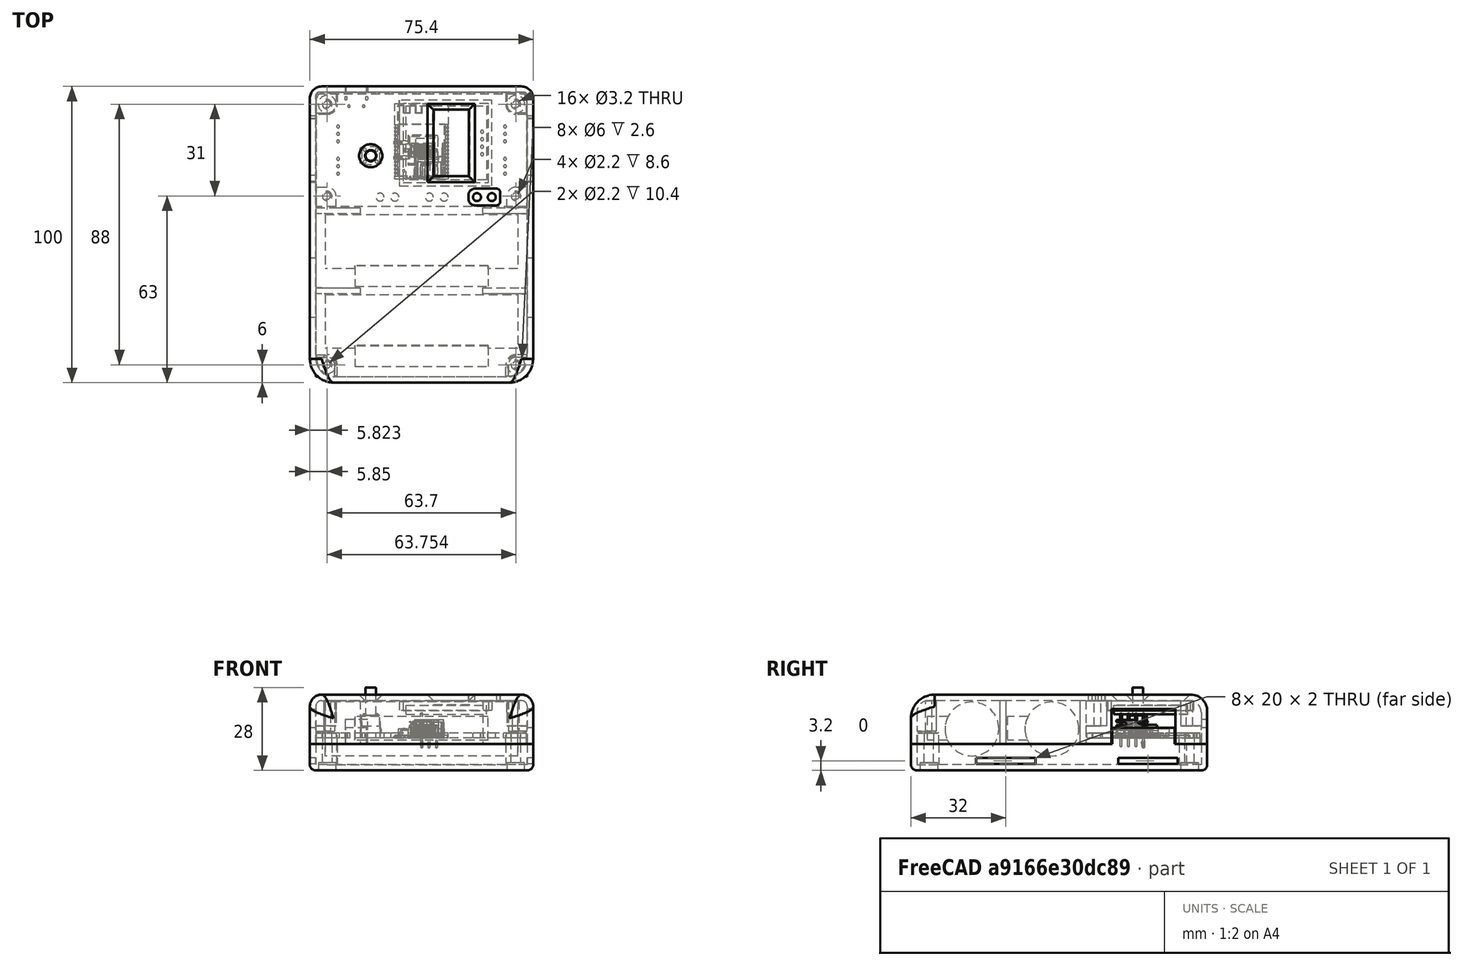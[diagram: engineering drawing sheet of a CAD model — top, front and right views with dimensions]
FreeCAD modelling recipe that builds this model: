
FCSTD DOCUMENT  (FreeCAD 0.21R33694 (Git))
Label: rwled
License: All rights reserved
LicenseURL: http://en.wikipedia.org/wiki/All_rights_reserved
objects: Part::Feature×61, App::Part×48, Sketcher::SketchObject×29, PartDesign::Pad×17, PartDesign::Pocket×12, PartDesign::Fillet×11, PartDesign::Body×6, Part::Part2DObjectPython×1, Mesh::Feature×1, App::DocumentObjectGroup×1
note: 177 computed .brp shape members not serialized (recipe doc carries the construction recipe); baked Part::Feature solids carry a one-line shape summary decoded from their .brp

FEATURE [Sketcher::SketchObject] Sketch
  FullyConstrained = true
  MapMode = 5
  Support = -> [XY_Plane043]
  sketch-geometry (4):
    g0: LineSegment StartX=-37.7 StartY=21.5 StartZ=0 EndX=37.7 EndY=21.5 EndZ=0
    g1: LineSegment StartX=37.7 StartY=21.5 StartZ=0 EndX=37.7 EndY=-78.5 EndZ=0
    g2: LineSegment StartX=37.7 StartY=-78.5 StartZ=0 EndX=-37.7 EndY=-78.5 EndZ=0
    g3: LineSegment StartX=-37.7 StartY=-78.5 StartZ=0 EndX=-37.7 EndY=21.5 EndZ=0
  constraints (11):
    c: Coincident(g0,g1)
    c: Coincident(g1,g2)
    c: Coincident(g2,g3)
    c: Coincident(g3,g0)
    c: Horizontal(g2)
    c: Vertical(g1)
    c: Vertical(g3)
    c: Symmetric(g0,g0,g-2)
    c: Distance(g0) = 75.4
    c: Distance(g0,g-1) = 21.5
    c: DistanceY(g3,g3) = 100
FEATURE [Part::Feature] Part__Feature049  label="Micro USB-B Female 5Pin SMD"
  shape: bbox 0.3 x 1.55 x 4.2 mm, 15 faces (baked)
FEATURE [Part::Feature] Part__Feature050  label="Micro USB-B Female 5Pin SMD001"
  shape: bbox 0.3 x 1.55 x 4.2 mm, 15 faces (baked)
FEATURE [Part::Feature] Part__Feature051  label="Micro USB-B Female 5Pin SMD002"
  shape: bbox 0.3 x 1.55 x 4.2 mm, 15 faces (baked)
FEATURE [Part::Feature] Part__Feature052  label="Micro USB-B Female 5Pin SMD003"
  shape: bbox 0.3 x 1.55 x 4.2 mm, 15 faces (baked)
FEATURE [Part::Feature] Part__Feature053  label="Micro USB-B Female 5Pin SMD004"
  shape: bbox 0.3 x 1.55 x 4.2 mm, 15 faces (baked)
FEATURE [Part::Feature] Part__Feature054  label="Micro USB-B Female 5Pin SMD005"
  shape: bbox 6.9 x 2.4 x 4.15 mm, 176 faces (baked)
FEATURE [Part::Feature] Part__Feature055  label="Micro USB-B Female 5Pin SMD006"
  shape: bbox 8.172 x 3.786 x 5.619 mm, 257 faces (baked)
FEATURE [App::Part] Micro_USB_B_Female_5Pin_SMD  label="Micro USB-B Female 5Pin SMD007"
  Group = -> [Part__Feature049,Part__Feature050,Part__Feature051,Part__Feature052,Part__Feature053,Part__Feature054,Part__Feature055]
  Origin = -> Origin087
  Placement = pos=(-22,14.6,4.85) rot=(0,1,1;3.14159rad)
FEATURE [Part::Feature] Part__Feature056  label="SW_PUSH_6mm_h13mm"
  Placement = pos=(-20.29,0.35,4) rot=(0,0,1;0rad)
  shape: bbox 7.174 x 6 x 16.5 mm, 105 faces (baked)
FEATURE [PartDesign::Pad] Pad
  Direction = (0,0,1)
  Length = 16.6
  Length2 = 10
  Profile = -> Sketch
  ReferenceAxis = -> Sketch [N_Axis]
  Type = 0
FEATURE [Sketcher::SketchObject] Sketch001
  FullyConstrained = true
  MapMode = 5
  Placement = pos=(0,0,0) rot=(0.57735,0.57735,0.57735;2.0944rad)
  Support = -> [YZ_Plane088]
  sketch-geometry (1):
    g0: Circle CenterX=9.1 CenterY=0 CenterZ=0 NormalX=0 NormalY=0 NormalZ=1 AngleXU=0 Radius=9.1
  constraints (3):
    c: PointOnObject(g0,g-1)
    c: Distance(g-1,g0) = 9.1
    c: PointOnObject(g-1,g0)
FEATURE [PartDesign::Pad] Pad001
  Direction = (1,-2e-16,3e-16)
  Length = 65
  Length2 = 10
  Placement = pos=(0,0,0) rot=(0.57735,0.57735,0.57735;2.0944rad)
  Profile = -> Sketch001
  ReferenceAxis = -> Sketch001 [N_Axis]
  Type = 0
FEATURE [Sketcher::SketchObject] Sketch002
  FullyConstrained = false
  MapMode = 5
  Placement = pos=(0,0,0) rot=(1,0,0;1.5708rad)
  Support = -> [XZ_Plane088]
  sketch-geometry (4):
    g0: LineSegment StartX=10 StartY=-3.77048 StartZ=0 EndX=55 EndY=-3.77048 EndZ=0
    g1: LineSegment StartX=55 StartY=-3.77048 StartZ=0 EndX=55 EndY=4.22952 EndZ=0
    g2: LineSegment StartX=55 StartY=4.22952 StartZ=0 EndX=10 EndY=4.22952 EndZ=0
    g3: LineSegment StartX=10 StartY=4.22952 StartZ=0 EndX=10 EndY=-3.77048 EndZ=0
  constraints (11):
    c: Coincident(g0,g1)
    c: Coincident(g1,g2)
    c: Coincident(g2,g3)
    c: Coincident(g3,g0)
    c: Horizontal(g0)
    c: Horizontal(g2)
    c: Vertical(g1)
    c: Vertical(g3)
    c: DistanceX(g-1,g0) = 10
    c: DistanceX(g2,g2) = 45
    c: DistanceY(g3,g3) = 8
FEATURE [PartDesign::Pad] Pad002
  BaseFeature = -> Pad001
  Direction = (0,-1,2e-16)
  Length = 6
  Length2 = 10
  Placement = pos=(0,0,0) rot=(0.57735,0.57735,0.57735;2.0944rad)
  Profile = -> Sketch002
  ReferenceAxis = -> Sketch002 [N_Axis]
  Type = 4
FEATURE [PartDesign::Body] Body001  label="accum-a"
  Group = -> [Sketch001,Pad001,Sketch002,Pad002]
  Origin = -> Origin088
  Placement = pos=(-32.5,-40,3) rot=(0,0,1;0rad)
  Tip = -> Pad002
FEATURE [Sketcher::SketchObject] Sketch003
  FullyConstrained = true
  MapMode = 5
  Placement = pos=(0,0,0) rot=(0.57735,0.57735,0.57735;2.0944rad)
  Support = -> [YZ_Plane090]
  sketch-geometry (1):
    g0: Circle CenterX=9.1 CenterY=0 CenterZ=0 NormalX=0 NormalY=0 NormalZ=1 AngleXU=0 Radius=9.1
  constraints (3):
    c: PointOnObject(g0,g-1)
    c: Distance(g-1,g0) = 9.1
    c: PointOnObject(g-1,g0)
FEATURE [PartDesign::Pad] Pad003
  Direction = (1,-2e-16,3e-16)
  Length = 65
  Length2 = 10
  Placement = pos=(0,0,0) rot=(0.57735,0.57735,0.57735;2.0944rad)
  Profile = -> Sketch003
  ReferenceAxis = -> Sketch003 [N_Axis]
  Type = 0
FEATURE [Sketcher::SketchObject] Sketch004
  FullyConstrained = false
  MapMode = 5
  Placement = pos=(0,0,0) rot=(1,0,0;1.5708rad)
  Support = -> [XZ_Plane090]
  sketch-geometry (4):
    g0: LineSegment StartX=10 StartY=-3.77048 StartZ=0 EndX=55 EndY=-3.77048 EndZ=0
    g1: LineSegment StartX=55 StartY=-3.77048 StartZ=0 EndX=55 EndY=4.22952 EndZ=0
    g2: LineSegment StartX=55 StartY=4.22952 StartZ=0 EndX=10 EndY=4.22952 EndZ=0
    g3: LineSegment StartX=10 StartY=4.22952 StartZ=0 EndX=10 EndY=-3.77048 EndZ=0
  constraints (11):
    c: Coincident(g0,g1)
    c: Coincident(g1,g2)
    c: Coincident(g2,g3)
    c: Coincident(g3,g0)
    c: Horizontal(g0)
    c: Horizontal(g2)
    c: Vertical(g1)
    c: Vertical(g3)
    c: DistanceX(g-1,g0) = 10
    c: DistanceX(g2,g2) = 45
    c: DistanceY(g3,g3) = 8
FEATURE [PartDesign::Pad] Pad004
  BaseFeature = -> Pad003
  Direction = (0,-1,2e-16)
  Length = 6
  Length2 = 10
  Placement = pos=(0,0,0) rot=(0.57735,0.57735,0.57735;2.0944rad)
  Profile = -> Sketch004
  ReferenceAxis = -> Sketch004 [N_Axis]
  Type = 4
FEATURE [PartDesign::Body] Body003  label="accum-b"
  Group = -> [Sketch003,Pad003,Sketch004,Pad004]
  Origin = -> Origin090
  Placement = pos=(-32.5,-67,3) rot=(0,0,1;0rad)
  Tip = -> Pad004
FEATURE [Sketcher::SketchObject] Sketch005
  ExternalGeometry = -> [Pad]
  FullyConstrained = true
  MapMode = 5
  Placement = pos=(0,0,0) rot=(1,0,0;3.14159rad)
  Support = -> [Pad]
  sketch-geometry (4):
    g0: LineSegment StartX=-35.7 StartY=76.5 StartZ=0 EndX=35.7 EndY=76.5 EndZ=0
    g1: LineSegment StartX=35.7 StartY=76.5 StartZ=0 EndX=35.7 EndY=-19.5 EndZ=0
    g2: LineSegment StartX=35.7 StartY=-19.5 StartZ=0 EndX=-35.7 EndY=-19.5 EndZ=0
    g3: LineSegment StartX=-35.7 StartY=-19.5 StartZ=0 EndX=-35.7 EndY=76.5 EndZ=0
  constraints (11):
    c: Coincident(g0,g1)
    c: Coincident(g1,g2)
    c: Coincident(g2,g3)
    c: Coincident(g3,g0)
    c: Horizontal(g2)
    c: Vertical(g1)
    c: Vertical(g3)
    c: DistanceX(g0,g0) = 71.4
    c: DistanceY(g3,g3) = 96
    c: Symmetric(g0,g0,g-2)
    c: DistanceY(g0,g-3) = 2
FEATURE [PartDesign::Pocket] Pocket
  BaseFeature = -> Pad
  Direction = (0,0,1)
  Length = 14.6
  Length2 = 5
  Profile = -> Sketch005
  ReferenceAxis = -> Sketch005 [N_Axis]
  Type = 0
FEATURE [Sketcher::SketchObject] Sketch006
  FullyConstrained = true
  MapMode = 5
  Placement = pos=(37.7,0,0) rot=(0.57735,0.57735,0.57735;2.0944rad)
  Support = -> [Pocket]
  sketch-geometry (4):
    g0: LineSegment StartX=-10.8 StartY=11.8 StartZ=0 EndX=10.8 EndY=11.8 EndZ=0
    g1: LineSegment StartX=10.8 StartY=11.8 StartZ=0 EndX=10.8 EndY=0 EndZ=0
    g2: LineSegment StartX=10.8 StartY=0 StartZ=0 EndX=-10.8 EndY=0 EndZ=0
    g3: LineSegment StartX=-10.8 StartY=0 StartZ=0 EndX=-10.8 EndY=11.8 EndZ=0
  constraints (12):
    c: Coincident(g0,g1)
    c: Coincident(g1,g2)
    c: Coincident(g2,g3)
    c: Coincident(g3,g0)
    c: Horizontal(g0)
    c: Horizontal(g2)
    c: Vertical(g1)
    c: Vertical(g3)
    c: DistanceX(g0,g0) = 21.6
    c: DistanceY(g3,g3) = 11.8
    c: Distance(g2,g-2) = 10.8
    c: PointOnObject(g-1,g2)
FEATURE [PartDesign::Pocket] Pocket001  label="Отверстие разъёмы справа"
  BaseFeature = -> Pocket
  Direction = (-1,0,0)
  Length = 2
  Length2 = 5
  Profile = -> Sketch006
  ReferenceAxis = -> Sketch006 [N_Axis]
  Type = 0
FEATURE [Sketcher::SketchObject] Sketch007
  FullyConstrained = true
  MapMode = 5
  Placement = pos=(-37.7,0,0) rot=(0.57735,-0.57735,-0.57735;2.0944rad)
  Support = -> [Pocket]
  sketch-geometry (4):
    g0: LineSegment StartX=-10.8 StartY=11.8 StartZ=0 EndX=10.8 EndY=11.8 EndZ=0
    g1: LineSegment StartX=10.8 StartY=11.8 StartZ=0 EndX=10.8 EndY=0 EndZ=0
    g2: LineSegment StartX=10.8 StartY=0 StartZ=0 EndX=-10.8 EndY=0 EndZ=0
    g3: LineSegment StartX=-10.8 StartY=0 StartZ=0 EndX=-10.8 EndY=11.8 EndZ=0
  constraints (12):
    c: Coincident(g0,g1)
    c: Coincident(g1,g2)
    c: Coincident(g2,g3)
    c: Coincident(g3,g0)
    c: Horizontal(g0)
    c: Horizontal(g2)
    c: Vertical(g1)
    c: Vertical(g3)
    c: DistanceX(g0,g0) = 21.6
    c: DistanceY(g3,g3) = 11.8
    c: Distance(g1,g-2) = 10.8
    c: PointOnObject(g-1,g2)
FEATURE [PartDesign::Pocket] Pocket002  label="Отверстие разъёмы слева"
  BaseFeature = -> Pocket001
  Direction = (1,0,0)
  Length = 2
  Length2 = 5
  Profile = -> Sketch007
  ReferenceAxis = -> Sketch007 [N_Axis]
  Type = 2
FEATURE [Sketcher::SketchObject] Sketch008
  ExternalGeometry = -> [Pocket]
  FullyConstrained = true
  MapMode = 5
  Placement = pos=(0,21.5,0) rot=(0,0.707107,0.707107;3.14159rad)
  Support = -> [Pocket]
  sketch-geometry (4):
    g0: LineSegment StartX=18.2 StartY=8.2 StartZ=0 EndX=25.8 EndY=8.2 EndZ=0
    g1: LineSegment StartX=25.8 StartY=8.2 StartZ=0 EndX=25.8 EndY=0 EndZ=0
    g2: LineSegment StartX=25.8 StartY=0 StartZ=0 EndX=18.2 EndY=0 EndZ=0
    g3: LineSegment StartX=18.2 StartY=0 StartZ=0 EndX=18.2 EndY=8.2 EndZ=0
  constraints (12):
    c: Coincident(g0,g1)
    c: Coincident(g1,g2)
    c: Coincident(g2,g3)
    c: Coincident(g3,g0)
    c: Horizontal(g0)
    c: Horizontal(g2)
    c: Vertical(g1)
    c: Vertical(g3)
    c: PointOnObject(g1,g-1)
    c: Distance(g-3,g1) = 11.9
    c: DistanceX(g0,g0) = 7.6
    c: DistanceY(g3,g3) = 8.2
FEATURE [PartDesign::Pocket] Pocket003  label="Отверстие usb"
  BaseFeature = -> Pocket002
  Direction = (0,-1,2e-16)
  Length = 2
  Length2 = 5
  Profile = -> Sketch008
  ReferenceAxis = -> Sketch008 [N_Axis]
  Type = 0
FEATURE [Sketcher::SketchObject] Sketch009
  FullyConstrained = false
  MapMode = 5
  Placement = pos=(0,0,16.6) rot=(0,0,1;0rad)
  Support = -> [Pocket]
  sketch-geometry (8):
    g0: LineSegment StartX=15.8257 StartY=-15.3377 StartZ=0 EndX=15.8257 EndY=-16.3217 EndZ=0
    g1: LineSegment StartX=26.545 StartY=-14.2196 StartZ=0 EndX=26.545 EndY=-17.3559 EndZ=0
    g2: LineSegment StartX=17.9219 StartY=-13.0027 StartZ=0 EndX=25.2742 EndY=-13.0027 EndZ=0
    g3: LineSegment StartX=17.897 StartY=-18.6636 StartZ=0 EndX=25.2824 EndY=-18.6636 EndZ=0
    g4: ArcOfCircle CenterX=18.1168 CenterY=-15.2861 CenterZ=0 NormalX=0 NormalY=0 NormalZ=1 AngleXU=0 Radius=2.29165 StartAngle=1.65595 EndAngle=3.16413
    g5: ArcOfCircle CenterX=18.1087 CenterY=-16.3895 CenterZ=0 NormalX=0 NormalY=0 NormalZ=1 AngleXU=0 Radius=2.28395 StartAngle=3.11191 EndAngle=4.61961
    g6: ArcOfCircle CenterX=25.295 CenterY=-14.253 CenterZ=0 NormalX=0 NormalY=0 NormalZ=1 AngleXU=0 Radius=1.25044 StartAngle=0.026699 EndAngle=1.58738
    g7: ArcOfCircle CenterX=25.2642 CenterY=-17.3827 CenterZ=0 NormalX=0 NormalY=0 NormalZ=1 AngleXU=0 Radius=1.28106 StartAngle=4.7266 EndAngle=6.30404
  constraints (12):
    c: Vertical(g0)
    c: Vertical(g1)
    c: Horizontal(g2)
    c: Horizontal(g3)
    c: Coincident(g4,g0)
    c: Coincident(g4,g2)
    c: Coincident(g5,g0)
    c: Coincident(g5,g3)
    c: Coincident(g6,g2)
    c: Coincident(g6,g1)
    c: Coincident(g7,g1)
    c: Coincident(g7,g3)
FEATURE [PartDesign::Pocket] Pocket004  label="Отверстия индикация"
  BaseFeature = -> Pocket003
  Direction = (0,0,-1)
  Length = 2
  Length2 = 5
  Profile = -> Sketch009
  ReferenceAxis = -> Sketch009 [N_Axis]
  Type = 0
FEATURE [Sketcher::SketchObject] Sketch010
  FullyConstrained = false
  MapMode = 5
  Placement = pos=(0,0,16.6) rot=(0,0,1;0rad)
  Support = -> [Pocket]
  sketch-geometry (7):
    g0: Circle CenterX=-17.1458 CenterY=-1.90076 CenterZ=0 NormalX=0 NormalY=0 NormalZ=1 AngleXU=0 Radius=3.9
    g1: GeomPoint X=-17.1369 Y=-1.89872 Z=0
    g2: GeomPoint X=-17.1369 Y=-1.89872 Z=0
    g3: LineSegment StartX=2 StartY=15.65 StartZ=0 EndX=18 EndY=15.65 EndZ=0
    g4: LineSegment StartX=18 StartY=15.65 StartZ=0 EndX=18 EndY=-10.85 EndZ=0
    g5: LineSegment StartX=18 StartY=-10.85 StartZ=0 EndX=2 EndY=-10.85 EndZ=0
    g6: LineSegment StartX=2 StartY=-10.85 StartZ=0 EndX=2 EndY=15.65 EndZ=0
  constraints (14):
    c: Diameter(g0) = 7.8
    c: Coincident(g2,g1)
    c: Coincident(g3,g4)
    c: Coincident(g4,g5)
    c: Coincident(g5,g6)
    c: Coincident(g6,g3)
    c: Horizontal(g3)
    c: Horizontal(g5)
    c: Vertical(g4)
    c: Vertical(g6)
    c: DistanceX(g3,g3) = 16
    c: DistanceY(g6,g6) = 26.5
    c: DistanceY(g5,g-1) = 10.85
    c: DistanceX(g-1,g5) = 2
FEATURE [Part::Part2DObjectPython] Circle  # Draft 2D object (typed FeaturePython)
  Area = 0.502819
  FirstAngle = 0
  LastAngle = 0
  MakeFace = true
  Placement = pos=(-17.14,-1.9,15) rot=(0,0,1;1.5708rad)
  Radius = 0.400065
FEATURE [PartDesign::Pocket] Pocket005  label="Отверстие кнопка (конус)"
  BaseFeature = -> Pocket004
  Direction = (0,0,-1)
  Length = 2
  Length2 = 5
  Profile = -> Sketch010
  ReferenceAxis = -> Sketch010 [N_Axis]
  TaperAngle = -45
  Type = 0
FEATURE [Sketcher::SketchObject] Sketch011
  ExternalGeometry = -> [Pocket]
  FullyConstrained = false
  MapMode = 5
  Placement = pos=(0,0,14.6) rot=(1,0,0;3.14159rad)
  Support = -> [Pocket]
  sketch-geometry (18):
    g0: LineSegment StartX=-35.7 StartY=46.5 StartZ=0 EndX=-20.7 EndY=46.5 EndZ=0
    g1: LineSegment StartX=-20.7 StartY=46.5 StartZ=0 EndX=-20.7 EndY=48.5 EndZ=0
    g2: LineSegment StartX=-20.7 StartY=48.5 StartZ=0 EndX=-35.7 EndY=48.5 EndZ=0
    g3: LineSegment StartX=-35.7 StartY=48.5 StartZ=0 EndX=-35.7 EndY=46.5 EndZ=0
    g4: LineSegment StartX=-35.7 StartY=19.5 StartZ=0 EndX=-20.7 EndY=19.5 EndZ=0
    g5: LineSegment StartX=-20.7 StartY=19.5 StartZ=0 EndX=-20.7 EndY=21.5 EndZ=0
    g6: LineSegment StartX=-20.7 StartY=21.5 StartZ=0 EndX=-35.7 EndY=21.5 EndZ=0
    g7: LineSegment StartX=-35.7 StartY=21.5 StartZ=0 EndX=-35.7 EndY=19.5 EndZ=0
    g8: LineSegment StartX=35.7 StartY=48.5 StartZ=0 EndX=20.7 EndY=48.5 EndZ=0
    g9: LineSegment StartX=20.7 StartY=48.5 StartZ=0 EndX=20.7 EndY=46.5 EndZ=0
    g10: LineSegment StartX=20.7 StartY=46.5 StartZ=0 EndX=35.7 EndY=46.5 EndZ=0
    g11: LineSegment StartX=35.7 StartY=46.5 StartZ=0 EndX=35.7 EndY=48.5 EndZ=0
    g12: LineSegment StartX=35.7 StartY=21.5 StartZ=0 EndX=20.7 EndY=21.5 EndZ=0
    g13: LineSegment StartX=20.7 StartY=21.5 StartZ=0 EndX=20.7 EndY=19.5 EndZ=0
    g14: LineSegment StartX=20.7 StartY=19.5 StartZ=0 EndX=35.7 EndY=19.5 EndZ=0
    g15: LineSegment StartX=35.7 StartY=19.5 StartZ=0 EndX=35.7 EndY=21.5 EndZ=0
    g16: GeomPoint X=-35.7 Y=47.5 Z=0
    g17: GeomPoint X=35.7 Y=47.5 Z=0
  constraints (48):
    c: Coincident(g0,g1)
    c: Coincident(g1,g2)
    c: Coincident(g2,g3)
    c: Coincident(g3,g0)
    c: Horizontal(g0)
    c: Horizontal(g2)
    c: Vertical(g1)
    c: Vertical(g3)
    c: PointOnObject(g0,g-3)
    c: Coincident(g4,g5)
    c: Coincident(g5,g6)
    c: Coincident(g6,g7)
    c: Coincident(g7,g4)
    c: Horizontal(g4)
    c: Horizontal(g6)
    c: Vertical(g5)
    c: Vertical(g7)
    c: Distance(g4,g5) = 2
    c: Distance(g0,g1) = 2
    c: Distance(g6) = 15
    c: Distance(g0) = 15
    c: Coincident(g8,g9)
    c: Coincident(g9,g10)
    c: Coincident(g10,g11)
    c: Coincident(g11,g8)
    c: Horizontal(g8)
    c: Horizontal(g10)
    c: Vertical(g9)
    c: Vertical(g11)
    c: PointOnObject(g8,g-4)
    c: Coincident(g12,g13)
    c: Coincident(g13,g14)
    c: Coincident(g14,g15)
    c: Coincident(g15,g12)
    c: Horizontal(g12)
    c: Horizontal(g14)
    c: Vertical(g13)
    c: Vertical(g15)
    c: Distance(g9) = 2
    c: Distance(g13) = 2
    c: Distance(g12) = 15
    c: Distance(g10) = 15
    c: Distance(g-3,g4) = 39
    c: Symmetric(g2,g0,g16)
    c: Symmetric(g8,g10,g17)
    c: Distance(g14,g-4) = 39
    c: Distance(g10,g12) = 25
    c: Distance(g0,g6) = 25
FEATURE [PartDesign::Pad] Pad005  label="Перегородки внутр"
  BaseFeature = -> Pocket005
  Direction = (0,0,-1)
  Length = 14.6
  Length2 = 10
  Profile = -> Sketch011
  ReferenceAxis = -> Sketch011 [N_Axis]
  Type = 0
FEATURE [Sketcher::SketchObject] Sketch012
  ExternalGeometry = -> [Pocket]
  FullyConstrained = true
  MapMode = 5
  Placement = pos=(0,0,14.6) rot=(1,0,0;3.14159rad)
  Support = -> [Pocket]
  sketch-geometry (24):
    g0: LineSegment StartX=-35.7 StartY=-12.5 StartZ=0 EndX=-31.85 EndY=-12.5 EndZ=0
    g1: LineSegment StartX=-28.85 StartY=-19.5 StartZ=0 EndX=-28.85 EndY=-15.5 EndZ=0
    g2: ArcOfCircle CenterX=-31.85 CenterY=-15.5 CenterZ=0 NormalX=0 NormalY=0 NormalZ=1 AngleXU=0 Radius=3 StartAngle=1e-16 EndAngle=1.5708
    g3: Circle CenterX=-31.85 CenterY=-15.5 CenterZ=0 NormalX=0 NormalY=0 NormalZ=1 AngleXU=0 Radius=1.1
    g4: LineSegment StartX=-28.85 StartY=-19.5 StartZ=0 EndX=-35.7 EndY=-19.5 EndZ=0
    g5: LineSegment StartX=-35.7 StartY=-12.5 StartZ=0 EndX=-35.7 EndY=-19.5 EndZ=0
    g6: Circle CenterX=31.85 CenterY=-15.5 CenterZ=0 NormalX=0 NormalY=0 NormalZ=1 AngleXU=0 Radius=1.1
    g7: LineSegment StartX=28.85 StartY=-19.5 StartZ=0 EndX=28.85 EndY=-15.5 EndZ=0
    g8: LineSegment StartX=35.7 StartY=-12.5 StartZ=0 EndX=31.85 EndY=-12.5 EndZ=0
    g9: ArcOfCircle CenterX=31.85 CenterY=-15.5 CenterZ=0 NormalX=0 NormalY=0 NormalZ=1 AngleXU=0 Radius=3 StartAngle=1.5708 EndAngle=3.14159
    g10: LineSegment StartX=35.7 StartY=-12.5 StartZ=0 EndX=35.7 EndY=-19.5 EndZ=0
    g11: LineSegment StartX=28.85 StartY=-19.5 StartZ=0 EndX=35.7 EndY=-19.5 EndZ=0
    g12: LineSegment StartX=-35.7 StartY=12.5 StartZ=0 EndX=-35.7 EndY=19.5 EndZ=0
    g13: LineSegment StartX=-35.7 StartY=19.5 StartZ=0 EndX=-28.85 EndY=19.5 EndZ=0
    g14: LineSegment StartX=-35.7 StartY=12.5 StartZ=0 EndX=-31.85 EndY=12.5 EndZ=0
    g15: LineSegment StartX=-28.85 StartY=19.5 StartZ=0 EndX=-28.85 EndY=15.5 EndZ=0
    g16: Circle CenterX=-31.85 CenterY=15.5 CenterZ=0 NormalX=0 NormalY=0 NormalZ=1 AngleXU=0 Radius=1.1
    g17: ArcOfCircle CenterX=-31.85 CenterY=15.5 CenterZ=0 NormalX=0 NormalY=0 NormalZ=1 AngleXU=0 Radius=3 StartAngle=4.71239 EndAngle=6.28319
    g18: LineSegment StartX=31.85 StartY=12.5 StartZ=0 EndX=35.7 EndY=12.5 EndZ=0
    g19: LineSegment StartX=35.7 StartY=12.5 StartZ=0 EndX=35.7 EndY=19.5 EndZ=0
    g20: LineSegment StartX=35.7 StartY=19.5 StartZ=0 EndX=28.85 EndY=19.5 EndZ=0
    g21: LineSegment StartX=28.85 StartY=19.5 StartZ=0 EndX=28.85 EndY=15.5 EndZ=0
    g22: Circle CenterX=31.85 CenterY=15.5 CenterZ=0 NormalX=0 NormalY=0 NormalZ=1 AngleXU=0 Radius=1.1
    g23: ArcOfCircle CenterX=31.85 CenterY=15.5 CenterZ=0 NormalX=0 NormalY=0 NormalZ=1 AngleXU=0 Radius=3 StartAngle=3.14159 EndAngle=4.71239
  constraints (71):
    c: PointOnObject(g0,g-5)
    c: Horizontal(g0)
    c: PointOnObject(g1,g-4)
    c: Vertical(g1)
    c: Coincident(g2,g0)
    c: Coincident(g2,g1)
    c: Distance(g2,g-4) = 4
    c: Distance(g2,g-5) = 3.85
    c: Coincident(g3,g2)
    c: Diameter(g3) = 2.2
    c: Distance(g0) = 3.85
    c: Distance(g1) = 4
    c: Coincident(g4,g1)
    c: Coincident(g4,g-5)
    c: Coincident(g5,g0)
    c: Coincident(g5,g4)
    c: Diameter(g2) = 6
    c: Diameter(g6) = 2.2
    c: Distance(g6,g-4) = 4
    c: Distance(g6,g-3) = 3.85
    c: PointOnObject(g7,g-4)
    c: Vertical(g7)
    c: PointOnObject(g8,g-3)
    c: Horizontal(g8)
    c: Distance(g7) = 4
    c: Distance(g8) = 3.85
    c: Coincident(g9,g6)
    c: Coincident(g9,g7)
    c: Coincident(g9,g8)
    c: Diameter(g9) = 6
    c: Coincident(g10,g8)
    c: Coincident(g10,g-4)
    c: Coincident(g11,g7)
    c: Coincident(g11,g10)
    c: PointOnObject(g12,g-5)
    c: PointOnObject(g12,g-5)
    c: Horizontal(g13)
    c: Coincident(g14,g12)
    c: Horizontal(g14)
    c: Coincident(g15,g13)
    c: Vertical(g15)
    c: Distance(g14) = 3.85
    c: Distance(g15) = 4
    c: Diameter(g16) = 2.2
    c: Distance(g16,g12) = 3.85
    c: Distance(g16,g13) = 4
    c: Distance(g13,g4) = 39
    c: Coincident(g17,g16)
    c: Coincident(g17,g15)
    c: Coincident(g17,g14)
    c: Diameter(g17) = 6
    c: Coincident(g13,g12)
    c: PointOnObject(g18,g-3)
    c: Horizontal(g18)
    c: PointOnObject(g19,g18)
    c: PointOnObject(g19,g-3)
    c: Vertical(g19)
    c: Horizontal(g20)
    c: Coincident(g21,g20)
    c: Vertical(g21)
    c: Distance(g18) = 3.85
    c: Distance(g21) = 4
    c: Diameter(g22) = 2.2
    c: Coincident(g20,g19)
    c: Distance(g19,g11) = 39
    c: Distance(g22,g19) = 3.85
    c: Distance(g22,g20) = 4
    c: Coincident(g23,g22)
    c: Coincident(g23,g18)
    c: Coincident(g23,g21)
    c: Diameter(g23) = 6
FEATURE [PartDesign::Pad] Pad006  label="Винты: под платой"
  BaseFeature = -> Pad005
  Direction = (0,0,-1)
  Length = 8.6
  Length2 = 10
  Profile = -> Sketch012
  ReferenceAxis = -> Sketch012 [N_Axis]
  Type = 0
FEATURE [Sketcher::SketchObject] Sketch013
  ExternalGeometry = -> [Pocket]
  FullyConstrained = true
  MapMode = 5
  Placement = pos=(0,0,14.6) rot=(1,0,0;3.14159rad)
  Support = -> [Pocket]
  sketch-geometry (12):
    g0: LineSegment StartX=-35.7 StartY=76.5 StartZ=0 EndX=-29.35 EndY=76.5 EndZ=0
    g1: LineSegment StartX=-35.7 StartY=76.5 StartZ=0 EndX=-35.7 EndY=70 EndZ=0
    g2: LineSegment StartX=-35.7 StartY=70 StartZ=0 EndX=-31.85 EndY=70 EndZ=0
    g3: LineSegment StartX=-29.35 StartY=76.5 StartZ=0 EndX=-29.35 EndY=72.5 EndZ=0
    g4: Circle CenterX=-31.85 CenterY=72.5 CenterZ=0 NormalX=0 NormalY=0 NormalZ=1 AngleXU=0 Radius=1.1
    g5: ArcOfCircle CenterX=-31.85 CenterY=72.5 CenterZ=0 NormalX=0 NormalY=0 NormalZ=1 AngleXU=0 Radius=2.5 StartAngle=4.71239 EndAngle=6.28319
    g6: LineSegment StartX=35.7 StartY=76.5 StartZ=0 EndX=35.7 EndY=70 EndZ=0
    g7: LineSegment StartX=35.7 StartY=76.5 StartZ=0 EndX=29.35 EndY=76.5 EndZ=0
    g8: LineSegment StartX=29.35 StartY=76.5 StartZ=0 EndX=29.35 EndY=72.5 EndZ=0
    g9: LineSegment StartX=35.7 StartY=70 StartZ=0 EndX=31.85 EndY=70 EndZ=0
    g10: Circle CenterX=31.85 CenterY=72.5 CenterZ=0 NormalX=0 NormalY=0 NormalZ=1 AngleXU=0 Radius=1.1
    g11: ArcOfCircle CenterX=31.85 CenterY=72.5 CenterZ=0 NormalX=0 NormalY=0 NormalZ=1 AngleXU=0 Radius=2.5 StartAngle=3.14159 EndAngle=4.71239
  constraints (35):
    c: PointOnObject(g0,g-4)
    c: PointOnObject(g0,g-4)
    c: Coincident(g1,g0)
    c: PointOnObject(g1,g-3)
    c: Vertical(g1)
    c: Coincident(g2,g1)
    c: Horizontal(g2)
    c: Distance(g2) = 3.85
    c: Coincident(g3,g0)
    c: Vertical(g3)
    c: Distance(g3) = 4
    c: Diameter(g4) = 2.2
    c: Distance(g4,g1) = 3.85
    c: Distance(g4,g0) = 4
    c: Coincident(g5,g4)
    c: Coincident(g5,g3)
    c: Coincident(g5,g2)
    c: Diameter(g5) = 5
    c: Coincident(g6,g-5)
    c: PointOnObject(g6,g-5)
    c: Coincident(g7,g6)
    c: PointOnObject(g7,g-4)
    c: Coincident(g8,g7)
    c: Vertical(g8)
    c: Coincident(g9,g6)
    c: Horizontal(g9)
    c: Distance(g9) = 3.85
    c: Distance(g8) = 4
    c: Diameter(g10) = 2.2
    c: Distance(g10,g7) = 4
    c: Distance(g10,g6) = 3.85
    c: Coincident(g11,g10)
    c: Coincident(g11,g9)
    c: Coincident(g11,g8)
    c: Diameter(g11) = 5
FEATURE [PartDesign::Pad] Pad007  label="Винты: низ"
  BaseFeature = -> Pad006
  Direction = (0,0,-1)
  Length = 10.4
  Length2 = 10
  Profile = -> Sketch013
  ReferenceAxis = -> Sketch013 [N_Axis]
  Type = 0
FEATURE [PartDesign::Fillet] Fillet  label="Сглаж: внутр боковые"
  Base = -> Pad007 [Edge64,Edge127,Edge157,Edge75,Edge145,Edge149]
  BaseFeature = -> Pad007
  Radius = 2
  SupportTransform = false
  UseAllEdges = false
FEATURE [PartDesign::Fillet] Fillet001  label="Сглаж: внутр - верх, низ"
  Base = -> Fillet [Edge55,Edge80]
  BaseFeature = -> Fillet
  Radius = 4
  SupportTransform = false
  UseAllEdges = false
FEATURE [PartDesign::Fillet] Fillet002  label="Сглаж: внутр углы верх"
  Base = -> Fillet001 [Edge5,Edge8]
  BaseFeature = -> Fillet001
  Radius = 1
  SupportTransform = false
  UseAllEdges = false
FEATURE [PartDesign::Fillet] Fillet003  label="Сглаж: внутр углы низ"
  Base = -> Fillet002 [Edge250,Edge255]
  BaseFeature = -> Fillet002
  Radius = 6
  SupportTransform = false
  UseAllEdges = false
FEATURE [PartDesign::Fillet] Fillet004  label="Сглаж: внеш - верх"
  Base = -> Fillet003 [Edge171]
  BaseFeature = -> Fillet003
  Radius = 5.5
  SupportTransform = false
  UseAllEdges = false
FEATURE [PartDesign::Fillet] Fillet005  label="Сглаж: внеш - плоскость, бок верх"
  Base = -> Fillet004 [Edge25,Edge10,Edge4,Edge1]
  BaseFeature = -> Fillet004
  Radius = 4
  SupportTransform = false
  UseAllEdges = false
FEATURE [Sketcher::SketchObject] Sketch014
  FullyConstrained = true
  MapMode = 5
  Support = -> [XY_Plane091]
  sketch-geometry (4):
    g0: LineSegment StartX=-37.7 StartY=21.5 StartZ=0 EndX=37.7 EndY=21.5 EndZ=0
    g1: LineSegment StartX=37.7 StartY=21.5 StartZ=0 EndX=37.7 EndY=-78.5 EndZ=0
    g2: LineSegment StartX=37.7 StartY=-78.5 StartZ=0 EndX=-37.7 EndY=-78.5 EndZ=0
    g3: LineSegment StartX=-37.7 StartY=-78.5 StartZ=0 EndX=-37.7 EndY=21.5 EndZ=0
  constraints (11):
    c: Coincident(g0,g1)
    c: Coincident(g1,g2)
    c: Coincident(g2,g3)
    c: Coincident(g3,g0)
    c: Horizontal(g2)
    c: Vertical(g1)
    c: Vertical(g3)
    c: DistanceY(g3,g3) = 100
    c: DistanceX(g0,g0) = 75.4
    c: Symmetric(g0,g0,g-2)
    c: Distance(g0,g-1) = 21.5
FEATURE [PartDesign::Pad] Pad008
  Direction = (0,0,1)
  Length = 9
  Length2 = 10
  Profile = -> Sketch014
  ReferenceAxis = -> Sketch014 [N_Axis]
  Reversed = true
  Type = 0
FEATURE [Sketcher::SketchObject] Sketch015
  ExternalGeometry = -> [Pad008]
  FullyConstrained = true
  MapMode = 5
  Support = -> [Pad008]
  sketch-geometry (4):
    g0: LineSegment StartX=-35.7 StartY=19.5 StartZ=0 EndX=35.7 EndY=19.5 EndZ=0
    g1: LineSegment StartX=35.7 StartY=19.5 StartZ=0 EndX=35.7 EndY=-76.5 EndZ=0
    g2: LineSegment StartX=35.7 StartY=-76.5 StartZ=0 EndX=-35.7 EndY=-76.5 EndZ=0
    g3: LineSegment StartX=-35.7 StartY=-76.5 StartZ=0 EndX=-35.7 EndY=19.5 EndZ=0
  constraints (12):
    c: Coincident(g0,g1)
    c: Coincident(g1,g2)
    c: Coincident(g2,g3)
    c: Coincident(g3,g0)
    c: Horizontal(g0)
    c: Horizontal(g2)
    c: Vertical(g1)
    c: Vertical(g3)
    c: Distance(g0,g-3) = 2
    c: Distance(g0,g-4) = 2
    c: Distance(g0,g-5) = 2
    c: Distance(g1,g-6) = 2
FEATURE [PartDesign::Pocket] Pocket006
  BaseFeature = -> Pad008
  Direction = (0,0,-1)
  Length = 7
  Length2 = 5
  Profile = -> Sketch015
  ReferenceAxis = -> Sketch015 [N_Axis]
  Type = 0
FEATURE [Sketcher::SketchObject] Sketch016
  ExternalGeometry = -> [Pocket006]
  FullyConstrained = true
  MapMode = 5
  Support = -> [Pocket006]
  sketch-geometry (12):
    g0: LineSegment StartX=-37.7 StartY=-10.6 StartZ=0 EndX=-35.7 EndY=-10.6 EndZ=0
    g1: LineSegment StartX=-35.7 StartY=-10.6 StartZ=0 EndX=-35.7 EndY=10.6 EndZ=0
    g2: LineSegment StartX=-35.7 StartY=10.6 StartZ=0 EndX=-37.7 EndY=10.6 EndZ=0
    g3: LineSegment StartX=-37.7 StartY=10.6 StartZ=0 EndX=-37.7 EndY=-10.6 EndZ=0
    g4: LineSegment StartX=35.7 StartY=-10.6 StartZ=0 EndX=37.7 EndY=-10.6 EndZ=0
    g5: LineSegment StartX=37.7 StartY=-10.6 StartZ=0 EndX=37.7 EndY=10.6 EndZ=0
    g6: LineSegment StartX=37.7 StartY=10.6 StartZ=0 EndX=35.7 EndY=10.6 EndZ=0
    g7: LineSegment StartX=35.7 StartY=10.6 StartZ=0 EndX=35.7 EndY=-10.6 EndZ=0
    g8: LineSegment StartX=-25.6 StartY=19.5 StartZ=0 EndX=-18.4 EndY=19.5 EndZ=0
    g9: LineSegment StartX=-18.4 StartY=19.5 StartZ=0 EndX=-18.4 EndY=21.5 EndZ=0
    g10: LineSegment StartX=-18.4 StartY=21.5 StartZ=0 EndX=-25.6 EndY=21.5 EndZ=0
    g11: LineSegment StartX=-25.6 StartY=21.5 StartZ=0 EndX=-25.6 EndY=19.5 EndZ=0
  constraints (36):
    c: Coincident(g0,g1)
    c: Coincident(g1,g2)
    c: Coincident(g2,g3)
    c: Coincident(g3,g0)
    c: Horizontal(g0)
    c: Horizontal(g2)
    c: Vertical(g1)
    c: Vertical(g3)
    c: Coincident(g4,g5)
    c: Coincident(g5,g6)
    c: Coincident(g6,g7)
    c: Coincident(g7,g4)
    c: Horizontal(g4)
    c: Horizontal(g6)
    c: Vertical(g5)
    c: Vertical(g7)
    c: Coincident(g8,g9)
    c: Coincident(g9,g10)
    c: Coincident(g10,g11)
    c: Coincident(g11,g8)
    c: Horizontal(g8)
    c: Horizontal(g10)
    c: Vertical(g9)
    c: Vertical(g11)
    c: PointOnObject(g6,g-8)
    c: PointOnObject(g5,g-7)
    c: PointOnObject(g8,g-4)
    c: PointOnObject(g9,g-6)
    c: PointOnObject(g2,g-5)
    c: PointOnObject(g1,g-3)
    c: DistanceX(g8,g8) = 7.2
    c: Distance(g10,g-6) = 12.1
    c: DistanceY(g3,g3) = 21.2
    c: Distance(g2,g-1) = 10.6
    c: Distance(g6,g-1) = 10.6
    c: DistanceY(g5,g5) = 21.2
FEATURE [PartDesign::Pad] Pad009  label="Прикрытие боковых отверстий1"
  BaseFeature = -> Pocket006
  Direction = (0,0,1)
  Length = 5.4
  Length2 = 10
  Profile = -> Sketch016
  ReferenceAxis = -> Sketch016 [N_Axis]
  Type = 0
FEATURE [Sketcher::SketchObject] Sketch017
  ExternalGeometry = -> [Pad009]
  FullyConstrained = true
  MapMode = 5
  Placement = pos=(37.7,0,0) rot=(0.57735,0.57735,0.57735;2.0944rad)
  Support = -> [Pad009]
  sketch-geometry (8):
    g0: LineSegment StartX=-56.5 StartY=-4.8 StartZ=0 EndX=-36.5 EndY=-4.8 EndZ=0
    g1: LineSegment StartX=-36.5 StartY=-4.8 StartZ=0 EndX=-36.5 EndY=-6.8 EndZ=0
    g2: LineSegment StartX=-36.5 StartY=-6.8 StartZ=0 EndX=-56.5 EndY=-6.8 EndZ=0
    g3: LineSegment StartX=-56.5 StartY=-6.8 StartZ=0 EndX=-56.5 EndY=-4.8 EndZ=0
    g4: LineSegment StartX=-8.5 StartY=-4.8 StartZ=0 EndX=11.5 EndY=-4.8 EndZ=0
    g5: LineSegment StartX=11.5 StartY=-4.8 StartZ=0 EndX=11.5 EndY=-6.8 EndZ=0
    g6: LineSegment StartX=11.5 StartY=-6.8 StartZ=0 EndX=-8.5 EndY=-6.8 EndZ=0
    g7: LineSegment StartX=-8.5 StartY=-6.8 StartZ=0 EndX=-8.5 EndY=-4.8 EndZ=0
  constraints (24):
    c: Coincident(g0,g1)
    c: Coincident(g1,g2)
    c: Coincident(g2,g3)
    c: Coincident(g3,g0)
    c: Horizontal(g0)
    c: Horizontal(g2)
    c: Vertical(g1)
    c: Vertical(g3)
    c: Coincident(g4,g5)
    c: Coincident(g5,g6)
    c: Coincident(g6,g7)
    c: Coincident(g7,g4)
    c: Horizontal(g4)
    c: Horizontal(g6)
    c: Vertical(g5)
    c: Vertical(g7)
    c: DistanceX(g0,g0) = 20
    c: DistanceX(g4,g4) = 20
    c: DistanceY(g3,g3) = 2
    c: DistanceY(g7,g7) = 2
    c: DistanceX(g5,g-3) = 10
    c: DistanceX(g1,g6) = 28
    c: DistanceY(g-3,g5) = 2.2
    c: DistanceY(g-3,g1) = 2.2
FEATURE [PartDesign::Pocket] Pocket007  label="Отверстия под ремни1"
  BaseFeature = -> Pad009
  Direction = (-1,0,0)
  Length = 5
  Length2 = 5
  Profile = -> Sketch017
  ReferenceAxis = -> Sketch017 [N_Axis]
  Type = 1
FEATURE [Sketcher::SketchObject] Sketch018
  ExternalGeometry = -> [Pocket007]
  FullyConstrained = false
  MapMode = 5
  Placement = pos=(0,0,-7) rot=(0,0,1;0rad)
  Support = -> [Pocket007]
  sketch-geometry (24):
    g0: LineSegment StartX=-31.85 StartY=12.1 StartZ=0 EndX=-35.7 EndY=12.1 EndZ=0
    g1: LineSegment StartX=-35.7 StartY=12.1 StartZ=0 EndX=-35.7 EndY=19.5 EndZ=0
    g2: LineSegment StartX=-35.7 StartY=19.5 StartZ=0 EndX=-28.5639 EndY=19.5 EndZ=0
    g3: LineSegment StartX=-28.5639 StartY=19.5 StartZ=0 EndX=-28.5639 EndY=14.6272 EndZ=0
    g4: Circle CenterX=-31.85 CenterY=15.5 CenterZ=0 NormalX=0 NormalY=0 NormalZ=1 AngleXU=0 Radius=1.6
    g5: ArcOfCircle CenterX=-31.85 CenterY=15.5 CenterZ=0 NormalX=0 NormalY=0 NormalZ=1 AngleXU=0 Radius=3.4 StartAngle=4.71239 EndAngle=6.02359
    g6: LineSegment StartX=28.45 StartY=19.5 StartZ=0 EndX=35.7 EndY=19.5 EndZ=0
    g7: LineSegment StartX=35.7 StartY=19.5 StartZ=0 EndX=35.7 EndY=12.1 EndZ=0
    g8: LineSegment StartX=35.7 StartY=12.1 StartZ=0 EndX=31.85 EndY=12.1 EndZ=0
    g9: LineSegment StartX=28.45 StartY=19.5 StartZ=0 EndX=28.45 EndY=15.5 EndZ=0
    g10: Circle CenterX=31.85 CenterY=15.5 CenterZ=0 NormalX=0 NormalY=0 NormalZ=1 AngleXU=0 Radius=1.6
    g11: ArcOfCircle CenterX=31.85 CenterY=15.5 CenterZ=0 NormalX=0 NormalY=0 NormalZ=1 AngleXU=0 Radius=3.4 StartAngle=3.14159 EndAngle=4.71239
    g12: LineSegment StartX=35.7 StartY=-69.1 StartZ=0 EndX=35.7 EndY=-76.5 EndZ=0
    g13: LineSegment StartX=35.7 StartY=-76.5 StartZ=0 EndX=28.45 EndY=-76.5 EndZ=0
    g14: LineSegment StartX=28.45 StartY=-76.5 StartZ=0 EndX=28.45 EndY=-72.5 EndZ=0
    g15: LineSegment StartX=35.7 StartY=-69.1 StartZ=0 EndX=31.85 EndY=-69.1 EndZ=0
    g16: Circle CenterX=31.85 CenterY=-72.5 CenterZ=0 NormalX=0 NormalY=0 NormalZ=1 AngleXU=0 Radius=1.6
    g17: ArcOfCircle CenterX=31.85 CenterY=-72.5 CenterZ=0 NormalX=0 NormalY=0 NormalZ=1 AngleXU=0 Radius=3.4 StartAngle=1.5708 EndAngle=3.14159
    g18: LineSegment StartX=-35.7 StartY=-76.5 StartZ=0 EndX=-28.45 EndY=-76.5 EndZ=0
    g19: LineSegment StartX=-35.7 StartY=-76.5 StartZ=0 EndX=-35.7 EndY=-69.1 EndZ=0
    g20: LineSegment StartX=-35.7 StartY=-69.1 StartZ=0 EndX=-31.85 EndY=-69.1 EndZ=0
    g21: LineSegment StartX=-28.45 StartY=-76.5 StartZ=0 EndX=-28.45 EndY=-72.5 EndZ=0
    g22: Circle CenterX=-31.85 CenterY=-72.5 CenterZ=0 NormalX=0 NormalY=0 NormalZ=1 AngleXU=0 Radius=1.6
    g23: ArcOfCircle CenterX=-31.85 CenterY=-72.5 CenterZ=0 NormalX=0 NormalY=0 NormalZ=1 AngleXU=0 Radius=3.4 StartAngle=1.9e-15 EndAngle=1.5708
  constraints (65):
    c: PointOnObject(g0,g-5)
    c: Horizontal(g0)
    c: Coincident(g1,g0)
    c: Coincident(g1,g-5)
    c: Coincident(g2,g1)
    c: PointOnObject(g2,g-4)
    c: Vertical(g3)
    c: Diameter(g4) = 3.2
    c: DistanceX(g0,g0) = 3.85
    c: Distance(g4,g1) = 3.85
    c: Distance(g4,g2) = 4
    c: Coincident(g5,g4)
    c: Coincident(g5,g3)
    c: Coincident(g5,g0)
    c: Diameter(g5) = 6.8
    c: PointOnObject(g6,g-4)
    c: Coincident(g6,g-4)
    c: PointOnObject(g7,g-3)
    c: Horizontal(g8)
    c: Coincident(g9,g6)
    c: Vertical(g9)
    c: Diameter(g10) = 3.2
    c: DistanceY(g9,g9) = 4
    c: DistanceX(g8,g8) = 3.85
    c: Distance(g10,g6) = 4
    c: Coincident(g11,g10)
    c: Coincident(g11,g9)
    c: Coincident(g11,g8)
    c: Diameter(g11) = 6.8
    c: PointOnObject(g12,g-3)
    c: Coincident(g12,g-6)
    c: Coincident(g13,g12)
    c: PointOnObject(g13,g-6)
    c: Coincident(g14,g13)
    c: Vertical(g14)
    c: Coincident(g15,g12)
    c: Horizontal(g15)
    c: Diameter(g16) = 3.2
    c: DistanceY(g14,g14) = 4
    c: DistanceX(g15,g15) = 3.85
    c: Distance(g16,g-6) = 4
    c: Distance(g16,g-3) = 3.85
    c: Coincident(g17,g16)
    c: Coincident(g17,g14)
    c: Coincident(g17,g15)
    c: Diameter(g17) = 6.8
    c: Coincident(g18,g-6)
    c: PointOnObject(g18,g-6)
    c: Coincident(g19,g18)
    c: PointOnObject(g19,g-5)
    c: Coincident(g20,g19)
    c: Horizontal(g20)
    c: Coincident(g21,g18)
    c: Vertical(g21)
    c: Diameter(g22) = 3.2
    c: DistanceX(g20,g20) = 3.85
    c: DistanceY(g21,g21) = 4
    c: Distance(g22,g-6) = 4
    c: Distance(g22,g-5) = 3.85
    c: Coincident(g23,g22)
    c: Coincident(g23,g20)
    c: Coincident(g23,g21)
    c: Diameter(g23) = 6.8
    c: Coincident(g2,g3)
    c: Coincident(g7,g6)
FEATURE [PartDesign::Pad] Pad010  label="Винты"
  BaseFeature = -> Pocket007
  Direction = (0,0,1)
  Length = 7
  Length2 = 10
  Profile = -> Sketch018
  ReferenceAxis = -> Sketch018 [N_Axis]
  Type = 0
FEATURE [Sketcher::SketchObject] Sketch019
  ExternalGeometry = -> [Pad010]
  FullyConstrained = true
  MapMode = 5
  Placement = pos=(0,0,-9) rot=(1,0,0;3.14159rad)
  Support = -> [Pad010]
  sketch-geometry (4):
    g0: Circle CenterX=-31.85 CenterY=72.5 CenterZ=0 NormalX=0 NormalY=0 NormalZ=1 AngleXU=0 Radius=3
    g1: Circle CenterX=31.85 CenterY=72.5 CenterZ=0 NormalX=0 NormalY=0 NormalZ=1 AngleXU=0 Radius=3
    g2: Circle CenterX=-31.85 CenterY=-15.5 CenterZ=0 NormalX=0 NormalY=0 NormalZ=1 AngleXU=0 Radius=3
    g3: Circle CenterX=31.85 CenterY=-15.5 CenterZ=0 NormalX=0 NormalY=0 NormalZ=1 AngleXU=0 Radius=3
  constraints (12):
    c: Diameter(g0) = 6
    c: Diameter(g1) = 6
    c: Diameter(g2) = 6
    c: Diameter(g3) = 6
    c: DistanceY(g-5,g2) = 6
    c: DistanceY(g-6,g3) = 6
    c: DistanceY(g0,g-3) = 6
    c: DistanceY(g1,g-4) = 6
    c: DistanceX(g1,g-4) = 5.85
    c: DistanceX(g-3,g0) = 5.85
    c: DistanceX(g-5,g2) = 5.85
    c: DistanceX(g3,g-6) = 5.85
FEATURE [PartDesign::Pocket] Pocket008  label="Углубления винтов1"
  BaseFeature = -> Pad010
  Direction = (0,0,1)
  Length = 2.6
  Length2 = 5
  Profile = -> Sketch019
  ReferenceAxis = -> Sketch019 [N_Axis]
  Type = 0
FEATURE [PartDesign::Fillet] Fillet006  label="Сглаж: внеш боковые верх"
  Base = -> Pocket008 [Edge2,Edge1]
  BaseFeature = -> Pocket008
  Radius = 4
  SupportTransform = false
  UseAllEdges = false
FEATURE [PartDesign::Fillet] Fillet007  label="Сглаж: внеш боковые низ"
  Base = -> Fillet006 [Edge39,Edge79]
  BaseFeature = -> Fillet006
  Radius = 8
  SupportTransform = false
  UseAllEdges = false
FEATURE [PartDesign::Fillet] Fillet008  label="Сглаж: внеш плоскость1"
  Base = -> Fillet007 [Edge3,Edge4,Edge5,Edge6,Edge7,Edge8,Edge1,Edge2]
  BaseFeature = -> Fillet007
  Radius = 2
  SupportTransform = false
  UseAllEdges = false
FEATURE [PartDesign::Body] Body004  label="down-old"
  Group = -> [Sketch014,Pad008,Sketch015,Pocket006,Sketch016,Pad009,Sketch017,Pocket007,Sketch018,Pad010,Sketch019,Pocket008,Fillet006,Fillet007,Fillet008]
  Origin = -> Origin091
  Placement = pos=(0,0,-2) rot=(0,0,1;0rad)
  Tip = -> Fillet008
FEATURE [Mesh::Feature] XT30F
  Placement = pos=(13.9,-13.9,15) rot=(0.707107,0,-0.707107;3.14159rad)
FEATURE [Part::Feature] Part__Feature  label="SOLID"
  shape: bbox 2 x 1.2 x 0.45 mm, 26 faces (baked)
FEATURE [App::Part] R_0805_2012Metric
  Group = -> [Part__Feature]
  Origin = -> Origin
  Placement = pos=(-11.049,5.588,1.65) rot=(0,0,-1;1.5708rad)
FEATURE [Part::Feature] Part__Feature057  label="SOLID001"
  shape: bbox 7.5 x 4.6 x 2 mm, 40 faces (baked)
FEATURE [App::Part] CP_EIA_7343_20_Kemet_V  label="CP_EIA-7343-20_Kemet-V"
  Group = -> [Part__Feature057]
  Origin = -> Origin092
  Placement = pos=(-15.24,10.16,1.65) rot=(0,0,1;3.14159rad)
FEATURE [Part::Feature] Part__Feature058  label="SOLID002"
  shape: bbox 2.8 x 2.9 x 1.55 mm, 109 faces (baked)
FEATURE [App::Part] SOT_23_5  label="SOT-23-5"
  Group = -> [Part__Feature058]
  Origin = -> Origin093
  Placement = pos=(-20.8225,5.588,1.65) rot=(0,0,1;0rad)
FEATURE [Part::Feature] Part__Feature059  label="SOLID003"
  shape: bbox 2 x 1.2 x 0.45 mm, 26 faces (baked)
FEATURE [App::Part] R_0805_2012Metric001
  Group = -> [Part__Feature059]
  Origin = -> Origin094
  Placement = pos=(-24.003,5.588,1.65) rot=(0,0,-1;1.5708rad)
FEATURE [Part::Feature] Part__Feature060  label="SOLID004"
  shape: bbox 2 x 1.2 x 0.45 mm, 26 faces (baked)
FEATURE [App::Part] R_0805_2012Metric002
  Group = -> [Part__Feature060]
  Origin = -> Origin095
  Placement = pos=(17.399,11.176,1.65) rot=(0,0,1;1.5708rad)
FEATURE [Part::Feature] Part__Feature061  label="SOLID005"
  shape: bbox 9.9 x 11.5 x 9.5 mm, 137 faces (baked)
FEATURE [App::Part] JST_XH_S3B_XH_A_1x03_P2_50mm_Horizontal  label="JST_XH_S3B-XH-A_1x03_P2.50mm_Horizontal"
  Group = -> [Part__Feature061]
  Origin = -> Origin096
  Placement = pos=(28.194,-7.961,1.65) rot=(0,0,1;1.5708rad)
FEATURE [Part::Feature] Part__Feature062  label="SOLID006"
  shape: bbox 2 x 1.25 x 1.25 mm, 28 faces (baked)
FEATURE [App::Part] C_0805_2012Metric
  Group = -> [Part__Feature062]
  Origin = -> Origin097
  Placement = pos=(11.303,5.255,1.65) rot=(0,0,-1;1.5708rad)
FEATURE [Part::Feature] Part__Feature063  label="SOLID007"
  shape: bbox 9.9 x 11.5 x 9.5 mm, 137 faces (baked)
FEATURE [App::Part] JST_XH_S3B_XH_A_1x03_P2_50mm_Horizontal001  label="JST_XH_S3B-XH-A_1x03_P2.50mm_Horizontal001"
  Group = -> [Part__Feature063]
  Origin = -> Origin098
  Placement = pos=(-28.173,-2.961,1.65) rot=(0,0,-1;1.5708rad)
FEATURE [Part::Feature] Part__Feature064  label="SOLID008"
  shape: bbox 2 x 1.25 x 1.25 mm, 28 faces (baked)
FEATURE [App::Part] C_0805_2012Metric001
  Group = -> [Part__Feature064]
  Origin = -> Origin099
  Placement = pos=(-13.208,5.588,1.65) rot=(0,0,-1;1.5708rad)
FEATURE [Part::Feature] Part__Feature065  label="SOLID009"
  shape: bbox 18 x 25.5 x 3.1 mm, 751 faces (baked)
FEATURE [App::Part] ESP32_WROOM_32  label="ESP32-WROOM-32"
  Group = -> [Part__Feature065]
  Origin = -> Origin100
  Placement = pos=(0.172,3.155,1.65) rot=(0,0,1;0rad)
FEATURE [Part::Feature] Part__Feature066  label="SOLID010"
  shape: bbox 2.5 x 2 x 0.78 mm, 48 faces (baked)
FEATURE [App::Part] Bosch_LGA_8_2x2_5mm_P0_65mm_ClockwisePinNumbering  label="Bosch_LGA-8_2x2.5mm_P0.65mm_ClockwisePinNumbering"
  Group = -> [Part__Feature066]
  Origin = -> Origin101
  Placement = pos=(15.329,5.293,1.65) rot=(0,0,-1;1.5708rad)
FEATURE [Part::Feature] Part__Feature067  label="SOLID011"
  shape: bbox 9.9 x 11.5 x 9.5 mm, 137 faces (baked)
FEATURE [App::Part] JST_XH_S3B_XH_A_1x03_P2_50mm_Horizontal002  label="JST_XH_S3B-XH-A_1x03_P2.50mm_Horizontal002"
  Group = -> [Part__Feature067]
  Origin = -> Origin102
  Placement = pos=(28.194,2.961,1.65) rot=(0,0,1;1.5708rad)
FEATURE [Part::Feature] Part__Feature068  label="SOLID012"
  shape: bbox 2 x 1.25 x 1.25 mm, 28 faces (baked)
FEATURE [App::Part] C_0805_2012Metric002
  Group = -> [Part__Feature068]
  Origin = -> Origin103
  Placement = pos=(-17.526,5.588,1.65) rot=(0,0,-1;1.5708rad)
FEATURE [Part::Feature] Part__Feature069  label="SOLID013"
  shape: bbox 9.9 x 11.5 x 9.5 mm, 137 faces (baked)
FEATURE [App::Part] JST_XH_S3B_XH_A_1x03_P2_50mm_Horizontal003  label="JST_XH_S3B-XH-A_1x03_P2.50mm_Horizontal003"
  Group = -> [Part__Feature069]
  Origin = -> Origin104
  Placement = pos=(-28.173,7.961,1.65) rot=(0,0,-1;1.5708rad)
FEATURE [Part::Feature] Part__Feature070  label="SOLID014"
  shape: bbox 2.54 x 10.16 x 11.54 mm, 100 faces (baked)
FEATURE [App::Part] PinHeader_1x04_P2_54mm_Vertical  label="PinHeader_1x04_P2.54mm_Vertical"
  Group = -> [Part__Feature070]
  Origin = -> Origin105
  Placement = pos=(20.447,6.223,1.65) rot=(0,0,1;0rad)
FEATURE [Part::Feature] Part__Feature071  label="SOLID015"
  shape: bbox 2 x 1.25 x 1.25 mm, 28 faces (baked)
FEATURE [App::Part] C_0805_2012Metric003
  Group = -> [Part__Feature071]
  Origin = -> Origin106
  Placement = pos=(-19.558,2.667,1.65) rot=(0,0,1;0rad)
FEATURE [Part::Feature] Part__Feature072  label="SOLID016"
  shape: bbox 2 x 1.2 x 0.45 mm, 26 faces (baked)
FEATURE [App::Part] R_0805_2012Metric003
  Group = -> [Part__Feature072]
  Origin = -> Origin107
  Placement = pos=(-15.3615,5.608,1.65) rot=(0,0,-1;1.5708rad)
FEATURE [Part::Feature] Part__Feature073  label="SOLID017"
  shape: bbox 2 x 1.2 x 0.45 mm, 26 faces (baked)
FEATURE [App::Part] R_0805_2012Metric004
  Group = -> [Part__Feature073]
  Origin = -> Origin108
  Placement = pos=(15.367,11.176,1.65) rot=(0,0,-1;1.5708rad)
FEATURE [Part::Feature] Part__Feature074  label="SOLID018"
  shape: bbox 2.5 x 3 x 1.2 mm, 76 faces (baked)
FEATURE [App::Part] SOT_23  label="SOT-23"
  Group = -> [Part__Feature074]
  Origin = -> Origin109
  Placement = pos=(12.3675,11.176,1.65) rot=(0,0,1;3.14159rad)
FEATURE [Part::Feature] Part__Feature075  label="SOLID019"
  shape: bbox 2 x 1.2 x 0.45 mm, 26 faces (baked)
FEATURE [App::Part] R_0805_2012Metric005
  Group = -> [Part__Feature075]
  Origin = -> Origin110
  Placement = pos=(-2.286,9.779,-0.05) rot=(0.707107,-0.707107,0;3.14159rad)
FEATURE [Part::Feature] Part__Feature076  label="SOLID020"
  shape: bbox 2 x 1.2 x 0.45 mm, 26 faces (baked)
FEATURE [App::Part] R_0805_2012Metric006
  Group = -> [Part__Feature076]
  Origin = -> Origin111
  Placement = pos=(-6.858,-0.381,-0.05) rot=(0,1,0;3.14159rad)
FEATURE [Part::Feature] Part__Feature077  label="SOLID021"
  shape: bbox 4 x 4 x 0.77 mm, 158 faces (baked)
FEATURE [App::Part] QFN_24_1EP_4x4mm_P0_5mm_EP2_6x2_6mm  label="QFN-24-1EP_4x4mm_P0.5mm_EP2.6x2.6mm"
  Group = -> [Part__Feature077]
  Origin = -> Origin112
  Placement = pos=(-12.6675,11.918,-0.05) rot=(1,0,0;3.14159rad)
FEATURE [Part::Feature] Part__Feature078  label="SOLID022"
  shape: bbox 5 x 2.7 x 2.22 mm, 41 faces (baked)
FEATURE [App::Part] D_SMA
  Group = -> [Part__Feature078]
  Origin = -> Origin113
  Placement = pos=(16.4018,-10.668,-0.05) rot=(1,0,0;3.14159rad)
FEATURE [Part::Feature] Part__Feature079  label="SOLID023"
  shape: bbox 5 x 2.7 x 2.22 mm, 41 faces (baked)
FEATURE [App::Part] D_SMA001
  Group = -> [Part__Feature079]
  Origin = -> Origin114
  Placement = pos=(-7.017,-10.668,-0.05) rot=(1,0,0;3.14159rad)
FEATURE [Part::Feature] Part__Feature080  label="SOLID024"
  shape: bbox 2.5 x 1.25 x 1.1 mm, 67 faces (baked)
FEATURE [App::Part] D_SOD_323  label="D_SOD-323"
  Group = -> [Part__Feature080]
  Origin = -> Origin115
  Placement = pos=(-17.1958,5.8252,-0.05) rot=(0.707107,-0.707107,0;3.14159rad)
FEATURE [Part::Feature] Part__Feature081  label="SOLID025"
  shape: bbox 2 x 1.25 x 1.25 mm, 28 faces (baked)
FEATURE [App::Part] C_0805_2012Metric004
  Group = -> [Part__Feature081]
  Origin = -> Origin116
  Placement = pos=(-4.003,5.461,-0.05) rot=(0,1,0;3.14159rad)
FEATURE [Part::Feature] Part__Feature082  label="SOLID026"
  shape: bbox 2 x 1.2 x 0.45 mm, 26 faces (baked)
FEATURE [App::Part] R_0805_2012Metric007
  Group = -> [Part__Feature082]
  Origin = -> Origin117
  Placement = pos=(-6.4535,16.129,-0.05) rot=(0,1,0;3.14159rad)
FEATURE [Part::Feature] Part__Feature083  label="COMPOUND"
  shape: bbox 9.25 x 10 x 4.4 mm, 13 faces (baked)
FEATURE [Part::Feature] Part__Feature084  label="COMPOUND001"
  shape: bbox 7.55 x 10 x 1.27 mm, 12 faces (baked)
FEATURE [Part::Feature] Part__Feature085  label="COMPOUND002"
  shape: bbox 4.95 x 1.24 x 2.95 mm, 22 faces (baked)
FEATURE [Part::Feature] Part__Feature086  label="COMPOUND003"
  shape: bbox 1.3 x 1.24 x 0.5 mm, 10 faces (baked)
FEATURE [Part::Feature] Part__Feature087  label="COMPOUND004"
  shape: bbox 4.95 x 1.24 x 2.95 mm, 22 faces (baked)
FEATURE [App::Part] COMPOUND  label="COMPOUND005"
  Group = -> [Part__Feature083,Part__Feature084,Part__Feature085,Part__Feature086,Part__Feature087]
  Origin = -> Origin118
FEATURE [App::Part] TO_263_2  label="TO-263-2"
  Group = -> [COMPOUND]
  Origin = -> Origin119
  Placement = pos=(5.099,-6.235,-0.05) rot=(0.707107,-0.707107,0;3.14159rad)
FEATURE [Part::Feature] Part__Feature088  label="SOLID027"
  shape: bbox 2 x 1.25 x 1.25 mm, 28 faces (baked)
FEATURE [App::Part] C_0805_2012Metric005
  Group = -> [Part__Feature088]
  Origin = -> Origin120
  Placement = pos=(-2.352,-6.731,-0.05) rot=(1,0,0;3.14159rad)
FEATURE [Part::Feature] Part__Feature089  label="SOLID028"
  shape: bbox 2 x 1.2 x 0.45 mm, 26 faces (baked)
FEATURE [App::Part] R_0805_2012Metric008
  Group = -> [Part__Feature089]
  Origin = -> Origin121
  Placement = pos=(-13.589,16.383,-0.05) rot=(0,1,0;3.14159rad)
FEATURE [Part::Feature] Part__Feature090  label="SOLID029"
  shape: bbox 2.5 x 1.25 x 1.1 mm, 67 faces (baked)
FEATURE [App::Part] D_SOD_324  label="D_SOD-324"
  Group = -> [Part__Feature090]
  Origin = -> Origin122
  Placement = pos=(-18.2118,10.287,-0.05) rot=(0,1,0;3.14159rad)
FEATURE [Part::Feature] Part__Feature091  label="SOLID030"
  shape: bbox 2 x 1.25 x 1.25 mm, 28 faces (baked)
FEATURE [App::Part] C_0805_2012Metric006
  Group = -> [Part__Feature091]
  Origin = -> Origin123
  Placement = pos=(-23.241,9.398,-0.05) rot=(0.707107,-0.707107,0;3.14159rad)
FEATURE [Part::Feature] Part__Feature092  label="SOLID031"
  shape: bbox 2 x 2 x 1.05 mm, 118 faces (baked)
FEATURE [App::Part] SOT_363_SC_70_6  label="SOT-363_SC-70-6"
  Group = -> [Part__Feature092]
  Origin = -> Origin124
  Placement = pos=(-2.418,-1.966,-0.05) rot=(0.707107,-0.707107,0;3.14159rad)
FEATURE [Part::Feature] Part__Feature093  label="SOLID032"
  shape: bbox 2 x 1.2 x 0.45 mm, 26 faces (baked)
FEATURE [App::Part] R_0805_2012Metric009
  Group = -> [Part__Feature093]
  Origin = -> Origin125
  Placement = pos=(3.4779,5.7404,-0.05) rot=(1,0,0;3.14159rad)
FEATURE [Part::Feature] Part__Feature094  label="SOLID033"
  shape: bbox 2 x 1.25 x 1.25 mm, 28 faces (baked)
FEATURE [App::Part] C_0805_2012Metric007
  Group = -> [Part__Feature094]
  Origin = -> Origin126
  Placement = pos=(-22.352,-14.544,-0.05) rot=(0.707107,-0.707107,0;3.14159rad)
FEATURE [Part::Feature] Part__Feature095  label="SOLID034"
  shape: bbox 1.6 x 3.2 x 0.5 mm, 206 faces (baked)
FEATURE [App::Part] R_Array_Convex_4x0603
  Group = -> [Part__Feature095]
  Origin = -> Origin127
  Placement = pos=(-8.117,2.597,-0.05) rot=(1,0,0;3.14159rad)
FEATURE [Part::Feature] Part__Feature096  label="SOLID035"
  shape: bbox 1.6 x 3.2 x 0.5 mm, 206 faces (baked)
FEATURE [App::Part] R_Array_Convex_4x0604
  Group = -> [Part__Feature096]
  Origin = -> Origin128
  Placement = pos=(-4.119,2.597,-0.05) rot=(1,0,0;3.14159rad)
FEATURE [Part::Feature] Part__Feature097  label="COMPOUND006"
  shape: bbox 9.25 x 10 x 4.4 mm, 13 faces (baked)
FEATURE [Part::Feature] Part__Feature098  label="COMPOUND007"
  shape: bbox 7.55 x 10 x 1.27 mm, 12 faces (baked)
FEATURE [Part::Feature] Part__Feature099  label="COMPOUND008"
  shape: bbox 4.95 x 1.24 x 2.95 mm, 22 faces (baked)
FEATURE [Part::Feature] Part__Feature100  label="COMPOUND009"
  shape: bbox 1.3 x 1.24 x 0.5 mm, 10 faces (baked)
FEATURE [Part::Feature] Part__Feature101  label="COMPOUND010"
  shape: bbox 4.95 x 1.24 x 2.95 mm, 22 faces (baked)
FEATURE [App::Part] COMPOUND001  label="COMPOUND011"
  Group = -> [Part__Feature097,Part__Feature098,Part__Feature099,Part__Feature100,Part__Feature101]
  Origin = -> Origin129
FEATURE [App::Part] TO_263_003  label="TO-263-003"
  Group = -> [COMPOUND001]
  Origin = -> Origin130
  Placement = pos=(-17.761,-6.235,-0.05) rot=(0.707107,-0.707107,0;3.14159rad)
FEATURE [Part::Feature] Part__Feature102  label="SOLID036"
  shape: bbox 2 x 1.2 x 0.45 mm, 26 faces (baked)
FEATURE [App::Part] R_0805_2012Metric010
  Group = -> [Part__Feature102]
  Origin = -> Origin131
  Placement = pos=(-2.352,-4.699,-0.05) rot=(0,1,0;3.14159rad)
FEATURE [Part::Feature] Part__Feature103  label="SOLID037"
  shape: bbox 2 x 2 x 1.05 mm, 118 faces (baked)
FEATURE [App::Part] SOT_363_SC_70_007  label="SOT-363_SC-70-007"
  Group = -> [Part__Feature103]
  Origin = -> Origin132
  Placement = pos=(-6.543,9.51,-0.05) rot=(0,1,0;3.14159rad)
FEATURE [Part::Feature] Part__Feature104  label="SOLID038"
  shape: bbox 2 x 1.2 x 0.45 mm, 26 faces (baked)
FEATURE [App::Part] R_0805_2012Metric011
  Group = -> [Part__Feature104]
  Origin = -> Origin133
  Placement = pos=(-6.4535,11.938,-0.05) rot=(0,1,0;3.14159rad)
FEATURE [Part::Feature] Part__Feature105  label="SOLID039"
  shape: bbox 2.5 x 1.25 x 1.1 mm, 67 faces (baked)
FEATURE [App::Part] D_SOD_325  label="D_SOD-325"
  Group = -> [Part__Feature105]
  Origin = -> Origin134
  Placement = pos=(3.5709,8.1534,-0.05) rot=(1,0,0;3.14159rad)
FEATURE [Part::Feature] Part__Feature106  label="SOLID040"
  shape: bbox 2 x 1.25 x 1.25 mm, 28 faces (baked)
FEATURE [App::Part] C_0805_2012Metric008
  Group = -> [Part__Feature106]
  Origin = -> Origin135
  Placement = pos=(-8.255,5.461,-0.05) rot=(0,1,0;3.14159rad)
FEATURE [Part::Feature] Part__Feature107  label="SOLID041"
  shape: bbox 2 x 1.2 x 0.45 mm, 26 faces (baked)
FEATURE [App::Part] R_0805_2012Metric012
  Group = -> [Part__Feature107]
  Origin = -> Origin136
  Placement = pos=(-6.4535,13.843,-0.05) rot=(0,1,0;3.14159rad)
FEATURE [Part::Feature] Part__Feature108  label="rwled-ctrl PCB"
  shape: bbox 70.87 x 38.1 x 1.6 mm, 74 faces (baked)
FEATURE [App::Part] rwled_ctrl_1  label="rwled-ctrl 1"
  Group = -> [R_0805_2012Metric,CP_EIA_7343_20_Kemet_V,SOT_23_5,R_0805_2012Metric001,R_0805_2012Metric002,JST_XH_S3B_XH_A_1x03_P2_50mm_Horizontal,C_0805_2012Metric,JST_XH_S3B_XH_A_1x03_P2_50mm_Horizontal001,C_0805_2012Metric001,ESP32_WROOM_32,Bosch_LGA_8_2x2_5mm_P0_65mm_ClockwisePinNumbering,JST_XH_S3B_XH_A_1x03_P2_50mm_Horizontal002,C_0805_2012Metric002,JST_XH_S3B_XH_A_1x03_P2_50mm_Horizontal003,+31 more]
  Origin = -> Origin137
  Placement = pos=(0,0,1.8) rot=(0,0,1;0rad)
FEATURE [Sketcher::SketchObject] Sketch020
  FullyConstrained = false
  MapMode = 5
  Support = -> [XY_Plane138]
  sketch-geometry (6):
    g0: LineSegment StartX=-5.23614 StartY=14.9128 StartZ=0 EndX=21.9639 EndY=14.9128 EndZ=0
    g1: LineSegment StartX=21.9639 StartY=14.9128 StartZ=0 EndX=21.9639 EndY=-10.0872 EndZ=0
    g2: LineSegment StartX=21.9639 StartY=-10.0872 StartZ=0 EndX=-5.23614 EndY=-10.0872 EndZ=0
    g3: LineSegment StartX=-5.23614 StartY=-10.0872 StartZ=0 EndX=-5.23614 EndY=14.9128 EndZ=0
    g4: GeomPoint X=21.4639 Y=2.41281 Z=0
    g5: GeomPoint X=21.9639 Y=2.41281 Z=0
  constraints (13):
    c: Coincident(g0,g1)
    c: Coincident(g1,g2)
    c: Coincident(g2,g3)
    c: Coincident(g3,g0)
    c: Horizontal(g0)
    c: Horizontal(g2)
    c: Vertical(g1)
    c: Vertical(g3)
    c: DistanceY(g3,g3) = 25
    c: DistanceX(g0,g0) = 27.2
    c: DistanceX(g4,g0) = 0.5
    c: Symmetric(g0,g1,g5)
    c: Horizontal(g5,g4)
FEATURE [PartDesign::Pad] Pad011
  Direction = (0,0,1)
  Length = 3
  Length2 = 10
  Profile = -> Sketch020
  ReferenceAxis = -> Sketch020 [N_Axis]
  Type = 0
FEATURE [Sketcher::SketchObject] Sketch021
  ExternalGeometry = -> [Pad011]
  FullyConstrained = true
  MapMode = 5
  Placement = pos=(0,0,3) rot=(0,0,1;0rad)
  Support = -> [Pad011]
  sketch-geometry (4):
    g0: LineSegment StartX=3.76386 StartY=13.9128 StartZ=0 EndX=16.2639 EndY=13.9128 EndZ=0
    g1: LineSegment StartX=16.2639 StartY=13.9128 StartZ=0 EndX=16.2639 EndY=-9.08719 EndZ=0
    g2: LineSegment StartX=16.2639 StartY=-9.08719 StartZ=0 EndX=3.76386 EndY=-9.08719 EndZ=0
    g3: LineSegment StartX=3.76386 StartY=-9.08719 StartZ=0 EndX=3.76386 EndY=13.9128 EndZ=0
  constraints (13):
    c: Coincident(g0,g1)
    c: Coincident(g1,g2)
    c: Coincident(g2,g3)
    c: Coincident(g3,g0)
    c: Horizontal(g0)
    c: Horizontal(g2)
    c: Vertical(g1)
    c: Vertical(g3)
    c: DistanceY(g1,g1) = 23
    c: DistanceY(g0,g-3) = 1
    c: DistanceX(g0,g0) = 12.5
    c: DistanceX(g0,g-3) = 5.7
    c: DistanceX(g-4,g0) = 9
FEATURE [PartDesign::Pad] Pad012
  BaseFeature = -> Pad011
  Direction = (0,0,1)
  Length = 0.2
  Length2 = 10
  Profile = -> Sketch021
  ReferenceAxis = -> Sketch021 [N_Axis]
  Type = 0
FEATURE [PartDesign::Body] Body005  label="display"
  Group = -> [Sketch020,Pad011,Sketch021,Pad012]
  Origin = -> Origin138
  Placement = pos=(0,0,8) rot=(0,0,1;0rad)
  Tip = -> Pad012
FEATURE [App::DocumentObjectGroup] Group
  Group = -> [Micro_USB_B_Female_5Pin_SMD,Part__Feature056,Body001,Body003,XT30F,Circle,rwled_ctrl_1,Body005]
FEATURE [Sketcher::SketchObject] Sketch022
  FullyConstrained = false
  MapMode = 5
  Placement = pos=(0,0,14.6) rot=(1,0,0;3.14159rad)
  Support = -> [Pad007]
  sketch-geometry (10):
    g0: LineSegment StartX=-6.24392 StartY=10.8872 StartZ=0 EndX=22.5561 EndY=10.8872 EndZ=0
    g1: LineSegment StartX=22.5561 StartY=10.8872 StartZ=0 EndX=22.5561 EndY=-15.7128 EndZ=0
    g2: LineSegment StartX=22.5561 StartY=-15.7128 StartZ=0 EndX=-6.24392 EndY=-15.7128 EndZ=0
    g3: LineSegment StartX=-6.24392 StartY=-15.7128 StartZ=0 EndX=-6.24392 EndY=10.8872 EndZ=0
    g4: LineSegment StartX=-7.44392 StartY=12.0872 StartZ=0 EndX=23.7561 EndY=12.0872 EndZ=0
    g5: LineSegment StartX=23.7561 StartY=12.0872 StartZ=0 EndX=23.7561 EndY=-16.9128 EndZ=0
    g6: LineSegment StartX=23.7561 StartY=-16.9128 StartZ=0 EndX=-7.44392 EndY=-16.9128 EndZ=0
    g7: LineSegment StartX=-7.44392 StartY=-16.9128 StartZ=0 EndX=-7.44392 EndY=12.0872 EndZ=0
    g8: GeomPoint X=21.7561 Y=10.0872 Z=0
    g9: GeomPoint X=21.7561 Y=-14.9128 Z=0
  constraints (26):
    c: Coincident(g0,g1)
    c: Coincident(g1,g2)
    c: Coincident(g2,g3)
    c: Coincident(g3,g0)
    c: Horizontal(g0)
    c: Horizontal(g2)
    c: Vertical(g1)
    c: Vertical(g3)
    c: Coincident(g4,g5)
    c: Coincident(g5,g6)
    c: Coincident(g6,g7)
    c: Coincident(g7,g4)
    c: Horizontal(g4)
    c: Horizontal(g6)
    c: Vertical(g5)
    c: Vertical(g7)
    c: DistanceY(g1,g1) = 26.6
    c: DistanceY(g0,g4) = 1.2
    c: DistanceX(g0,g4) = 1.2
    c: DistanceX(g4,g0) = 1.2
    c: DistanceY(g5,g1) = 1.2
    c: DistanceY(g9,g8) = 25
    c: Vertical(g8,g9)
    c: DistanceY(g8,g0) = 0.8
    c: DistanceX(g8,g0) = 0.8
    c: DistanceX(g0,g0) = 28.8
FEATURE [PartDesign::Pad] Pad013  label="зона дисплея"
  BaseFeature = -> Fillet005
  Direction = (0,0,-1)
  Length = 3.4
  Length2 = 10
  Profile = -> Sketch022
  ReferenceAxis = -> Sketch022 [N_Axis]
  Type = 0
FEATURE [PartDesign::Fillet] Fillet011  label="Сглаж: внеш - бок низ"
  Base = -> Pad013 [Edge32,Edge29,Edge8]
  BaseFeature = -> Pad013
  Radius = 8
  SupportTransform = false
  UseAllEdges = false
FEATURE [PartDesign::Body] Body  label="up"
  Group = -> [Sketch,Pad,Sketch005,Pocket,Sketch006,Pocket001,Sketch007,Pocket002,Sketch008,Pocket003,Sketch009,Pocket004,Sketch010,Pocket005,Sketch011,Pad005,Sketch012,Pad006,Sketch013,Pad007,Fillet,Fillet001,Fillet002,Fillet003,Fillet004,Fillet005,Sketch022,Pad013,Fillet011]
  Origin = -> Origin043
  Placement = pos=(0,0,-2) rot=(0,0,1;0rad)
  Tip = -> Fillet011
FEATURE [Sketcher::SketchObject] Sketch023
  FullyConstrained = true
  MapMode = 5
  Support = -> [XY_Plane139]
  sketch-geometry (8):
    g0: LineSegment StartX=-33.7 StartY=21.5 StartZ=0 EndX=33.7 EndY=21.5 EndZ=0
    g1: LineSegment StartX=37.7 StartY=17.5 StartZ=0 EndX=37.7 EndY=-70.5 EndZ=0
    g2: LineSegment StartX=29.7 StartY=-78.5 StartZ=0 EndX=-29.7 EndY=-78.5 EndZ=0
    g3: LineSegment StartX=-37.7 StartY=-70.5 StartZ=0 EndX=-37.7 EndY=17.5 EndZ=0
    g4: ArcOfCircle CenterX=33.7 CenterY=17.5 CenterZ=0 NormalX=0 NormalY=0 NormalZ=1 AngleXU=0 Radius=4 StartAngle=1e-16 EndAngle=1.5708
    g5: ArcOfCircle CenterX=-33.7 CenterY=17.5 CenterZ=0 NormalX=0 NormalY=0 NormalZ=1 AngleXU=0 Radius=4 StartAngle=1.5708 EndAngle=3.14159
    g6: ArcOfCircle CenterX=-29.7 CenterY=-70.5 CenterZ=0 NormalX=0 NormalY=0 NormalZ=1 AngleXU=0 Radius=8 StartAngle=3.14159 EndAngle=4.71239
    g7: ArcOfCircle CenterX=29.7 CenterY=-70.5 CenterZ=0 NormalX=0 NormalY=0 NormalZ=1 AngleXU=0 Radius=8 StartAngle=4.71239 EndAngle=6.28319
  constraints (19):
    c: Horizontal(g2)
    c: Vertical(g1)
    c: Vertical(g3)
    c: Tangent(g0,g4) = 1.5708
    c: Tangent(g1,g4) = 1.5708
    c: Tangent(g0,g5) = 1.5708
    c: Tangent(g3,g5) = 1.5708
    c: Tangent(g3,g6) = 1.5708
    c: Tangent(g2,g6) = 1.5708
    c: Tangent(g1,g7) = 1.5708
    c: Tangent(g2,g7) = 1.5708
    c: Equal(g6,g7)
    c: Equal(g5,g4)
    c: Distance(g0,g2) = 100
    c: Distance(g3,g1) = 75.4
    c: Distance(g0,g-1) = 21.5
    c: Radius(g5) = 4
    c: Symmetric(g3,g1,g-2)
    c: Radius(g6) = 8
FEATURE [PartDesign::Pad] Pad014
  Direction = (0,0,1)
  Length = 9
  Length2 = 10
  Profile = -> Sketch023
  ReferenceAxis = -> Sketch023 [N_Axis]
  Reversed = true
  Type = 0
FEATURE [PartDesign::Fillet] Fillet012  label="Сглаж: внеш плоскость"
  Base = -> Pad014 [Edge4]
  BaseFeature = -> Pad014
  Radius = 2
  SupportTransform = false
  UseAllEdges = false
FEATURE [Sketcher::SketchObject] Sketch024
  ExternalGeometry = -> [Fillet012]
  FullyConstrained = true
  MapMode = 5
  Placement = pos=(0,0,-9) rot=(1,0,0;3.14159rad)
  Support = -> [Fillet012]
  sketch-geometry (4):
    g0: Circle CenterX=-31.85 CenterY=72.5 CenterZ=0 NormalX=0 NormalY=0 NormalZ=1 AngleXU=0 Radius=3
    g1: Circle CenterX=31.85 CenterY=72.5 CenterZ=0 NormalX=0 NormalY=0 NormalZ=1 AngleXU=0 Radius=3
    g2: Circle CenterX=-31.85 CenterY=-15.5 CenterZ=0 NormalX=0 NormalY=0 NormalZ=1 AngleXU=0 Radius=3
    g3: Circle CenterX=31.85 CenterY=-15.5 CenterZ=0 NormalX=0 NormalY=0 NormalZ=1 AngleXU=0 Radius=3
  constraints (12):
    c: Diameter(g0) = 6
    c: Horizontal(g0,g1)
    c: Horizontal(g2,g3)
    c: Vertical(g0,g2)
    c: Vertical(g1,g3)
    c: Equal(g0,g1)
    c: Equal(g0,g2)
    c: Equal(g0,g3)
    c: Distance(g0,g-3) = 6
    c: Distance(g0,g-4) = 5.85
    c: Distance(g2,g-6) = 6
    c: Distance(g1,g-5) = 5.85
FEATURE [PartDesign::Pocket] Pocket009  label="Углубления винтов"
  BaseFeature = -> Fillet012
  Direction = (0,0,1)
  Length = 2.6
  Length2 = 5
  Profile = -> Sketch024
  ReferenceAxis = -> Sketch024 [N_Axis]
  Type = 0
FEATURE [Sketcher::SketchObject] Sketch025
  ExternalGeometry = -> [Pocket009]
  FullyConstrained = true
  MapMode = 5
  Support = -> [Pocket009]
  sketch-geometry (20):
    g0: LineSegment StartX=-31.85 StartY=12.1 StartZ=0 EndX=-35.7 EndY=12.1 EndZ=0
    g1: LineSegment StartX=-28.45 StartY=19.5 StartZ=0 EndX=-28.45 EndY=15.5 EndZ=0
    g2: Circle CenterX=-31.85 CenterY=15.5 CenterZ=0 NormalX=0 NormalY=0 NormalZ=1 AngleXU=0 Radius=1.6
    g3: ArcOfCircle CenterX=-31.85 CenterY=15.5 CenterZ=0 NormalX=0 NormalY=0 NormalZ=1 AngleXU=0 Radius=3.4 StartAngle=4.71239 EndAngle=6.28319
    g4: LineSegment StartX=35.7 StartY=12.1 StartZ=0 EndX=31.85 EndY=12.1 EndZ=0
    g5: LineSegment StartX=28.45 StartY=19.5 StartZ=0 EndX=28.45 EndY=15.5 EndZ=0
    g6: Circle CenterX=31.85 CenterY=15.5 CenterZ=0 NormalX=0 NormalY=0 NormalZ=1 AngleXU=0 Radius=1.6
    g7: ArcOfCircle CenterX=31.85 CenterY=15.5 CenterZ=0 NormalX=0 NormalY=0 NormalZ=1 AngleXU=0 Radius=3.4 StartAngle=3.14159 EndAngle=4.71239
    g8: LineSegment StartX=28.45 StartY=-76.5 StartZ=0 EndX=28.45 EndY=-72.5 EndZ=0
    g9: LineSegment StartX=35.7 StartY=-69.1 StartZ=0 EndX=31.85 EndY=-69.1 EndZ=0
    g10: Circle CenterX=31.85 CenterY=-72.5 CenterZ=0 NormalX=0 NormalY=0 NormalZ=1 AngleXU=0 Radius=1.6
    g11: ArcOfCircle CenterX=31.85 CenterY=-72.5 CenterZ=0 NormalX=0 NormalY=0 NormalZ=1 AngleXU=0 Radius=3.4 StartAngle=1.5708 EndAngle=3.14159
    g12: LineSegment StartX=-35.7 StartY=-69.1 StartZ=0 EndX=-31.85 EndY=-69.1 EndZ=0
    g13: LineSegment StartX=-28.45 StartY=-76.5 StartZ=0 EndX=-28.45 EndY=-72.5 EndZ=0
    g14: Circle CenterX=-31.85 CenterY=-72.5 CenterZ=0 NormalX=0 NormalY=0 NormalZ=1 AngleXU=0 Radius=1.6
    g15: ArcOfCircle CenterX=-31.85 CenterY=-72.5 CenterZ=0 NormalX=0 NormalY=0 NormalZ=1 AngleXU=0 Radius=3.4 StartAngle=1.8e-15 EndAngle=1.5708
    g16: LineSegment StartX=-35.7 StartY=12.1 StartZ=0 EndX=-35.7 EndY=-69.1 EndZ=0
    g17: LineSegment StartX=-28.45 StartY=-76.5 StartZ=0 EndX=28.45 EndY=-76.5 EndZ=0
    g18: LineSegment StartX=35.7 StartY=-69.1 StartZ=0 EndX=35.7 EndY=12.1 EndZ=0
    g19: LineSegment StartX=28.45 StartY=19.5 StartZ=0 EndX=-28.45 EndY=19.5 EndZ=0
  constraints (60):
    c: Horizontal(g0)
    c: Vertical(g1)
    c: Diameter(g2) = 3.2
    c: Coincident(g3,g2)
    c: Coincident(g3,g1)
    c: Coincident(g3,g0)
    c: Diameter(g3) = 6.8
    c: Horizontal(g4)
    c: Vertical(g5)
    c: Coincident(g7,g6)
    c: Coincident(g7,g5)
    c: Coincident(g7,g4)
    c: Vertical(g8)
    c: Horizontal(g9)
    c: Coincident(g11,g10)
    c: Coincident(g11,g8)
    c: Coincident(g11,g9)
    c: Horizontal(g12)
    c: Vertical(g13)
    c: Coincident(g15,g14)
    c: Coincident(g15,g12)
    c: Coincident(g15,g13)
    c: Coincident(g16,g0)
    c: Coincident(g16,g12)
    c: Vertical(g16)
    c: Coincident(g17,g13)
    c: Coincident(g17,g8)
    c: Horizontal(g17)
    c: Coincident(g18,g9)
    c: Coincident(g18,g4)
    c: Vertical(g18)
    c: Coincident(g19,g5)
    c: Coincident(g19,g1)
    c: Horizontal(g19)
    c: Equal(g2,g6)
    c: Equal(g2,g10)
    c: Equal(g2,g14)
    c: Equal(g3,g7)
    c: Equal(g3,g15)
    c: Equal(g3,g11)
    c: Horizontal(g2,g6)
    c: Horizontal(g14,g10)
    c: Vertical(g2,g14)
    c: Vertical(g6,g10)
    c: Distance(g2,g-4) = 5.85
    c: Distance(g2,g-3) = 6
    c: Distance(g6,g-5) = 5.85
    c: Distance(g0,g-4) = 2
    c: Distance(g1,g-3) = 2
    c: Distance(g4,g-5) = 2
    c: Distance(g13,g-6) = 2
    c: Equal(g0,g4)
    c: Vertical(g0,g12)
    c: Vertical(g2,g0)
    c: Horizontal(g13,g8)
    c: Horizontal(g14,g13)
    c: Distance(g14,g-6) = 6
    c: Vertical(g4,g9)
    c: Horizontal(g1,g5)
    c: Horizontal(g2,g1)
FEATURE [PartDesign::Pocket] Pocket010  label="Глубина"
  BaseFeature = -> Pocket009
  Direction = (0,0,-1)
  Length = 7
  Length2 = 5
  Profile = -> Sketch025
  ReferenceAxis = -> Sketch025 [N_Axis]
  Type = 0
FEATURE [Sketcher::SketchObject] Sketch026
  ExternalGeometry = -> [Pocket009]
  FullyConstrained = true
  MapMode = 5
  Support = -> [Pocket010]
  sketch-geometry (28):
    g0: LineSegment StartX=-31.85 StartY=12.1 StartZ=0 EndX=-35.4 EndY=12.1 EndZ=0
    g1: LineSegment StartX=-28.45 StartY=19.2 StartZ=0 EndX=-28.45 EndY=15.5 EndZ=0
    g2: Circle CenterX=-31.85 CenterY=15.5 CenterZ=0 NormalX=0 NormalY=0 NormalZ=1 AngleXU=0 Radius=1.6
    g3: ArcOfCircle CenterX=-31.85 CenterY=15.5 CenterZ=0 NormalX=0 NormalY=0 NormalZ=1 AngleXU=0 Radius=3.4 StartAngle=4.71239 EndAngle=6.28319
    g4: LineSegment StartX=35.4 StartY=12.1 StartZ=0 EndX=31.85 EndY=12.1 EndZ=0
    g5: LineSegment StartX=28.45 StartY=19.2 StartZ=0 EndX=28.45 EndY=15.5 EndZ=0
    g6: Circle CenterX=31.85 CenterY=15.5 CenterZ=0 NormalX=0 NormalY=0 NormalZ=1 AngleXU=0 Radius=1.6
    g7: ArcOfCircle CenterX=31.85 CenterY=15.5 CenterZ=0 NormalX=0 NormalY=0 NormalZ=1 AngleXU=0 Radius=3.4 StartAngle=3.14159 EndAngle=4.71239
    g8: LineSegment StartX=28.45 StartY=-76.2 StartZ=0 EndX=28.45 EndY=-72.5 EndZ=0
    g9: LineSegment StartX=35.4 StartY=-69.1 StartZ=0 EndX=31.85 EndY=-69.1 EndZ=0
    g10: Circle CenterX=31.85 CenterY=-72.5 CenterZ=0 NormalX=0 NormalY=0 NormalZ=1 AngleXU=0 Radius=1.6
    g11: ArcOfCircle CenterX=31.85 CenterY=-72.5 CenterZ=0 NormalX=0 NormalY=0 NormalZ=1 AngleXU=0 Radius=3.4 StartAngle=1.5708 EndAngle=3.14159
    g12: LineSegment StartX=-35.4 StartY=-69.1 StartZ=0 EndX=-31.85 EndY=-69.1 EndZ=0
    g13: LineSegment StartX=-28.45 StartY=-76.2 StartZ=0 EndX=-28.45 EndY=-72.5 EndZ=0
    g14: Circle CenterX=-31.85 CenterY=-72.5 CenterZ=0 NormalX=0 NormalY=0 NormalZ=1 AngleXU=0 Radius=1.6
    g15: ArcOfCircle CenterX=-31.85 CenterY=-72.5 CenterZ=0 NormalX=0 NormalY=0 NormalZ=1 AngleXU=0 Radius=3.4 StartAngle=4e-16 EndAngle=1.5708
    g16: LineSegment StartX=28.45 StartY=-76.2 StartZ=0 EndX=29.4 EndY=-76.2 EndZ=0
    g17: LineSegment StartX=-28.45 StartY=-76.2 StartZ=0 EndX=-29.4 EndY=-76.2 EndZ=0
    g18: LineSegment StartX=35.4 StartY=-69.1 StartZ=0 EndX=35.4 EndY=-70.2 EndZ=0
    g19: LineSegment StartX=-35.4 StartY=-69.1 StartZ=0 EndX=-35.4 EndY=-70.2 EndZ=0
    g20: LineSegment StartX=-35.4 StartY=12.1 StartZ=0 EndX=-35.4 EndY=17.2 EndZ=0
    g21: LineSegment StartX=-28.45 StartY=19.2 StartZ=0 EndX=-33.4 EndY=19.2 EndZ=0
    g22: LineSegment StartX=28.45 StartY=19.2 StartZ=0 EndX=33.4 EndY=19.2 EndZ=0
    g23: LineSegment StartX=35.4 StartY=12.1 StartZ=0 EndX=35.4 EndY=17.2 EndZ=0
    g24: ArcOfCircle CenterX=33.4 CenterY=17.2 CenterZ=0 NormalX=0 NormalY=0 NormalZ=1 AngleXU=0 Radius=2 StartAngle=0 EndAngle=1.5708
    g25: ArcOfCircle CenterX=-33.4 CenterY=17.2 CenterZ=0 NormalX=0 NormalY=0 NormalZ=1 AngleXU=0 Radius=2 StartAngle=1.5708 EndAngle=3.14159
    g26: ArcOfCircle CenterX=-29.4 CenterY=-70.2 CenterZ=0 NormalX=0 NormalY=0 NormalZ=1 AngleXU=0 Radius=6 StartAngle=3.14159 EndAngle=4.71239
    g27: ArcOfCircle CenterX=29.4 CenterY=-70.2 CenterZ=0 NormalX=0 NormalY=0 NormalZ=1 AngleXU=0 Radius=6 StartAngle=4.71239 EndAngle=6.28319
  constraints (80):
    c: Horizontal(g0)
    c: Vertical(g1)
    c: Diameter(g2) = 3.2
    c: Coincident(g3,g2)
    c: Coincident(g3,g1)
    c: Coincident(g3,g0)
    c: Diameter(g3) = 6.8
    c: Horizontal(g4)
    c: Vertical(g5)
    c: Coincident(g7,g6)
    c: Coincident(g7,g5)
    c: Coincident(g7,g4)
    c: Vertical(g8)
    c: Horizontal(g9)
    c: Coincident(g11,g10)
    c: Coincident(g11,g8)
    c: Coincident(g11,g9)
    c: Horizontal(g12)
    c: Vertical(g13)
    c: Coincident(g15,g14)
    c: Coincident(g15,g12)
    c: Coincident(g15,g13)
    c: Equal(g2,g6)
    c: Equal(g2,g10)
    c: Equal(g2,g14)
    c: Equal(g3,g7)
    c: Equal(g3,g15)
    c: Equal(g3,g11)
    c: Horizontal(g2,g6)
    c: Horizontal(g14,g10)
    c: Vertical(g2,g14)
    c: Vertical(g6,g10)
    c: Distance(g2,g-4) = 5.85
    c: Distance(g2,g-3) = 6
    c: Distance(g6,g-5) = 5.85
    c: Distance(g0,g-4) = 2.3
    c: Distance(g1,g-3) = 2.3
    c: Distance(g4,g-5) = 2.3
    c: Distance(g13,g-6) = 2.3
    c: Equal(g0,g4)
    c: Vertical(g0,g12)
    c: Vertical(g2,g0)
    c: Horizontal(g13,g8)
    c: Horizontal(g14,g13)
    c: Distance(g14,g-6) = 6
    c: Vertical(g4,g9)
    c: Horizontal(g1,g5)
    c: Horizontal(g2,g1)
    c: Horizontal(g13,g8)
    c: Horizontal(g1,g5)
    c: Vertical(g4,g9)
    c: Coincident(g16,g8)
    c: Horizontal(g16)
    c: Coincident(g17,g13)
    c: Horizontal(g17)
    c: Vertical(g0,g12)
    c: Coincident(g18,g9)
    c: Vertical(g18)
    c: Coincident(g19,g12)
    c: Vertical(g19)
    c: Coincident(g20,g0)
    c: Vertical(g20)
    c: Coincident(g21,g1)
    c: Horizontal(g21)
    c: Coincident(g22,g5)
    c: Horizontal(g22)
    c: Coincident(g23,g4)
    c: Vertical(g23)
    c: Tangent(g22,g24) = 1.5708
    c: Tangent(g23,g24) = -1.5708
    c: Tangent(g20,g25) = 1.5708
    c: Tangent(g21,g25) = -1.5708
    c: Tangent(g19,g26) = -1.5708
    c: Tangent(g17,g26) = 1.5708
    c: Tangent(g16,g27) = -1.5708
    c: Tangent(g18,g27) = 1.5708
    c: Equal(g26,g27)
    c: Equal(g25,g24)
    c: Radius(g25) = 2
    c: Radius(g26) = 6
FEATURE [PartDesign::Pad] Pad015  label="Стойки винтов + зазор с верхом"
  BaseFeature = -> Pocket010
  Direction = (0,0,1)
  Length = 3.6
  Length2 = 10
  Profile = -> Sketch026
  ReferenceAxis = -> Sketch026 [N_Axis]
  Type = 0
FEATURE [Sketcher::SketchObject] Sketch027
  ExternalGeometry = -> [Pocket006]
  FullyConstrained = true
  MapMode = 5
  Support = -> [Pad015]
  sketch-geometry (12):
    g0: LineSegment StartX=-37.7 StartY=-10.5 StartZ=0 EndX=-35.7 EndY=-10.5 EndZ=0
    g1: LineSegment StartX=-35.7 StartY=-10.5 StartZ=0 EndX=-35.7 EndY=10.5 EndZ=0
    g2: LineSegment StartX=-35.7 StartY=10.5 StartZ=0 EndX=-37.7 EndY=10.5 EndZ=0
    g3: LineSegment StartX=-37.7 StartY=10.5 StartZ=0 EndX=-37.7 EndY=-10.5 EndZ=0
    g4: LineSegment StartX=35.7 StartY=-10.5 StartZ=0 EndX=37.7 EndY=-10.5 EndZ=0
    g5: LineSegment StartX=37.7 StartY=-10.5 StartZ=0 EndX=37.7 EndY=10.5 EndZ=0
    g6: LineSegment StartX=37.7 StartY=10.5 StartZ=0 EndX=35.7 EndY=10.5 EndZ=0
    g7: LineSegment StartX=35.7 StartY=10.5 StartZ=0 EndX=35.7 EndY=-10.5 EndZ=0
    g8: LineSegment StartX=-25.5 StartY=19.5 StartZ=0 EndX=-18.5 EndY=19.5 EndZ=0
    g9: LineSegment StartX=-18.5 StartY=19.5 StartZ=0 EndX=-18.5 EndY=21.5 EndZ=0
    g10: LineSegment StartX=-18.5 StartY=21.5 StartZ=0 EndX=-25.5 EndY=21.5 EndZ=0
    g11: LineSegment StartX=-25.5 StartY=21.5 StartZ=0 EndX=-25.5 EndY=19.5 EndZ=0
  constraints (36):
    c: Coincident(g0,g1)
    c: Coincident(g1,g2)
    c: Coincident(g2,g3)
    c: Coincident(g3,g0)
    c: Horizontal(g0)
    c: Horizontal(g2)
    c: Vertical(g1)
    c: Vertical(g3)
    c: Coincident(g4,g5)
    c: Coincident(g5,g6)
    c: Coincident(g6,g7)
    c: Coincident(g7,g4)
    c: Horizontal(g4)
    c: Horizontal(g6)
    c: Vertical(g5)
    c: Vertical(g7)
    c: Coincident(g8,g9)
    c: Coincident(g9,g10)
    c: Coincident(g10,g11)
    c: Coincident(g11,g8)
    c: Horizontal(g8)
    c: Horizontal(g10)
    c: Vertical(g9)
    c: Vertical(g11)
    c: PointOnObject(g6,g-8)
    c: PointOnObject(g5,g-7)
    c: PointOnObject(g8,g-4)
    c: PointOnObject(g9,g-6)
    c: PointOnObject(g2,g-5)
    c: PointOnObject(g1,g-3)
    c: DistanceX(g8,g8) = 7
    c: Distance(g10,g-6) = 12.2
    c: DistanceY(g3,g3) = 21
    c: Distance(g2,g-1) = 10.5
    c: Horizontal(g1,g6)
    c: Horizontal(g0,g4)
FEATURE [PartDesign::Pad] Pad016  label="Прикрытие боковых отверстий"
  BaseFeature = -> Pad015
  Direction = (0,0,1)
  Length = 5.4
  Length2 = 10
  Profile = -> Sketch027
  ReferenceAxis = -> Sketch027 [N_Axis]
  Type = 0
FEATURE [Sketcher::SketchObject] Sketch028
  AttachmentOffset = pos=(0,0,40) rot=(0,0,1;0rad)
  ExternalGeometry = -> [Pad009]
  FullyConstrained = true
  MapMode = 5
  Placement = pos=(40,-8.9e-15,8.9e-15) rot=(0.57735,0.57735,0.57735;2.0944rad)
  Support = -> [YZ_Plane139]
  sketch-geometry (8):
    g0: LineSegment StartX=-56.5 StartY=-4.8 StartZ=0 EndX=-36.5 EndY=-4.8 EndZ=0
    g1: LineSegment StartX=-36.5 StartY=-4.8 StartZ=0 EndX=-36.5 EndY=-6.8 EndZ=0
    g2: LineSegment StartX=-36.5 StartY=-6.8 StartZ=0 EndX=-56.5 EndY=-6.8 EndZ=0
    g3: LineSegment StartX=-56.5 StartY=-6.8 StartZ=0 EndX=-56.5 EndY=-4.8 EndZ=0
    g4: LineSegment StartX=-8.5 StartY=-4.8 StartZ=0 EndX=11.5 EndY=-4.8 EndZ=0
    g5: LineSegment StartX=11.5 StartY=-4.8 StartZ=0 EndX=11.5 EndY=-6.8 EndZ=0
    g6: LineSegment StartX=11.5 StartY=-6.8 StartZ=0 EndX=-8.5 EndY=-6.8 EndZ=0
    g7: LineSegment StartX=-8.5 StartY=-6.8 StartZ=0 EndX=-8.5 EndY=-4.8 EndZ=0
  constraints (24):
    c: Coincident(g0,g1)
    c: Coincident(g1,g2)
    c: Coincident(g2,g3)
    c: Coincident(g3,g0)
    c: Horizontal(g0)
    c: Horizontal(g2)
    c: Vertical(g1)
    c: Vertical(g3)
    c: Coincident(g4,g5)
    c: Coincident(g5,g6)
    c: Coincident(g6,g7)
    c: Coincident(g7,g4)
    c: Horizontal(g4)
    c: Horizontal(g6)
    c: Vertical(g5)
    c: Vertical(g7)
    c: DistanceX(g0,g0) = 20
    c: DistanceX(g4,g4) = 20
    c: DistanceY(g3,g3) = 2
    c: DistanceY(g7,g7) = 2
    c: DistanceX(g5,g-3) = 10
    c: DistanceX(g1,g6) = 28
    c: DistanceY(g-3,g5) = 2.2
    c: DistanceY(g-3,g1) = 2.2
FEATURE [PartDesign::Pocket] Pocket011  label="Отверстия под ремни"
  BaseFeature = -> Pad016
  Direction = (-1,2e-16,-3e-16)
  Length = 5
  Length2 = 5
  Profile = -> Sketch028
  ReferenceAxis = -> Sketch028 [N_Axis]
  Type = 1
FEATURE [PartDesign::Body] Body006  label="down"
  Group = -> [Sketch023,Pad014,Fillet012,Sketch024,Pocket009,Sketch025,Pocket010,Sketch026,Pad015,Sketch027,Pad016,Sketch028,Pocket011]
  Origin = -> Origin139
  Placement = pos=(0,0,-2) rot=(0,0,1;0rad)
  Tip = -> Pocket011
